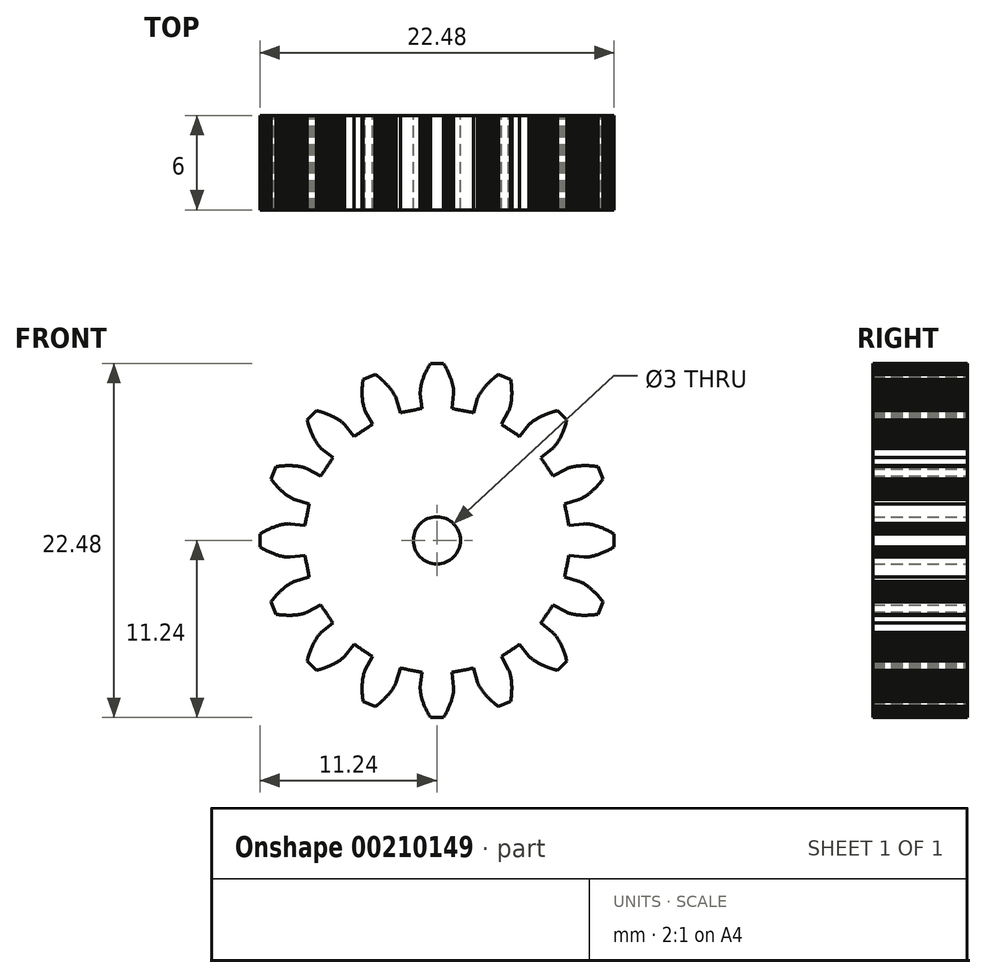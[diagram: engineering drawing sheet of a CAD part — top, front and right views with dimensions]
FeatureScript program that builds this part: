
annotation { "Feature Type Name" : "Feature", "Feature Type Description" : "" }
export const myFeature = defineFeature(function(context is Context, id is Id, definition is map)
    precondition{}
    {
        {
            var Q0;
            Q0=qCreatedBy(makeId("Front.planeOp"),FACE);
            var sketch = newSketch(context, id + "F0", { "sketchPlane" : qUnion([Q0])});
            skLineSegment(sketch, "E0", {"start": v(8.38, -0.95) * mm, "end": v(9.34, -1.06) * mm});
            skLineSegment(sketch, "E1", {"start": v(9.34, -1.06) * mm, "end": v(9.39, -1.06) * mm});
            skLineSegment(sketch, "E2", {"start": v(9.39, -1.06) * mm, "end": v(9.44, -1.06) * mm});
            skLineSegment(sketch, "E3", {"start": v(9.44, -1.06) * mm, "end": v(9.5, -1.06) * mm});
            skLineSegment(sketch, "E4", {"start": v(9.5, -1.06) * mm, "end": v(9.56, -1.05) * mm});
            skLineSegment(sketch, "E5", {"start": v(9.56, -1.05) * mm, "end": v(9.62, -1.05) * mm});
            skLineSegment(sketch, "E6", {"start": v(9.62, -1.05) * mm, "end": v(9.68, -1.04) * mm});
            skLineSegment(sketch, "E7", {"start": v(9.68, -1.04) * mm, "end": v(9.75, -1.03) * mm});
            skLineSegment(sketch, "E8", {"start": v(9.75, -1.03) * mm, "end": v(9.82, -1.01) * mm});
            skLineSegment(sketch, "E9", {"start": v(9.82, -1.01) * mm, "end": v(9.88, -1) * mm});
            skLineSegment(sketch, "E10", {"start": v(9.88, -1) * mm, "end": v(9.93, -0.99) * mm});
            skLineSegment(sketch, "E11", {"start": v(9.93, -0.99) * mm, "end": v(9.99, -0.97) * mm});
            skLineSegment(sketch, "E12", {"start": v(9.99, -0.97) * mm, "end": v(10.05, -0.95) * mm});
            skLineSegment(sketch, "E13", {"start": v(10.05, -0.95) * mm, "end": v(10.11, -0.93) * mm});
            skLineSegment(sketch, "E14", {"start": v(10.11, -0.93) * mm, "end": v(10.18, -0.91) * mm});
            skLineSegment(sketch, "E15", {"start": v(10.18, -0.91) * mm, "end": v(10.25, -0.9) * mm});
            skLineSegment(sketch, "E16", {"start": v(10.25, -0.9) * mm, "end": v(10.32, -0.87) * mm});
            skLineSegment(sketch, "E17", {"start": v(10.32, -0.87) * mm, "end": v(10.39, -0.84) * mm});
            skLineSegment(sketch, "E18", {"start": v(10.39, -0.84) * mm, "end": v(10.46, -0.8) * mm});
            skLineSegment(sketch, "E19", {"start": v(10.46, -0.8) * mm, "end": v(10.54, -0.78) * mm});
            skLineSegment(sketch, "E20", {"start": v(10.54, -0.78) * mm, "end": v(10.62, -0.74) * mm});
            skLineSegment(sketch, "E21", {"start": v(10.62, -0.74) * mm, "end": v(10.7, -0.7) * mm});
            skLineSegment(sketch, "E22", {"start": v(10.7, -0.7) * mm, "end": v(10.78, -0.67) * mm});
            skLineSegment(sketch, "E23", {"start": v(10.78, -0.67) * mm, "end": v(10.87, -0.63) * mm});
            skLineSegment(sketch, "E24", {"start": v(10.87, -0.63) * mm, "end": v(10.95, -0.58) * mm});
            skLineSegment(sketch, "E25", {"start": v(10.95, -0.58) * mm, "end": v(11.04, -0.53) * mm});
            skLineSegment(sketch, "E26", {"start": v(11.04, -0.53) * mm, "end": v(11.09, -0.5) * mm});
            skLineSegment(sketch, "E27", {"start": v(11.09, -0.5) * mm, "end": v(11.13, -0.48) * mm});
            skLineSegment(sketch, "E28", {"start": v(11.13, -0.48) * mm, "end": v(11.18, -0.46) * mm});
            skLineSegment(sketch, "E29", {"start": v(11.18, -0.46) * mm, "end": v(11.24, -0.42) * mm});
            skLineSegment(sketch, "E30", {"start": v(11.24, -0.42) * mm, "end": v(11.24, 0.42) * mm});
            skLineSegment(sketch, "E31", {"start": v(11.24, 0.42) * mm, "end": v(11.18, 0.46) * mm});
            skLineSegment(sketch, "E32", {"start": v(11.18, 0.46) * mm, "end": v(11.13, 0.48) * mm});
            skLineSegment(sketch, "E33", {"start": v(11.13, 0.48) * mm, "end": v(11.09, 0.5) * mm});
            skLineSegment(sketch, "E34", {"start": v(11.09, 0.5) * mm, "end": v(11.04, 0.53) * mm});
            skLineSegment(sketch, "E35", {"start": v(11.04, 0.53) * mm, "end": v(10.95, 0.58) * mm});
            skLineSegment(sketch, "E36", {"start": v(10.95, 0.58) * mm, "end": v(10.87, 0.63) * mm});
            skLineSegment(sketch, "E37", {"start": v(10.87, 0.63) * mm, "end": v(10.78, 0.67) * mm});
            skLineSegment(sketch, "E38", {"start": v(10.78, 0.67) * mm, "end": v(10.7, 0.7) * mm});
            skLineSegment(sketch, "E39", {"start": v(10.7, 0.7) * mm, "end": v(10.62, 0.74) * mm});
            skLineSegment(sketch, "E40", {"start": v(10.62, 0.74) * mm, "end": v(10.54, 0.78) * mm});
            skLineSegment(sketch, "E41", {"start": v(10.54, 0.78) * mm, "end": v(10.46, 0.8) * mm});
            skLineSegment(sketch, "E42", {"start": v(10.46, 0.8) * mm, "end": v(10.39, 0.84) * mm});
            skLineSegment(sketch, "E43", {"start": v(10.39, 0.84) * mm, "end": v(10.32, 0.87) * mm});
            skLineSegment(sketch, "E44", {"start": v(10.32, 0.87) * mm, "end": v(10.25, 0.9) * mm});
            skLineSegment(sketch, "E45", {"start": v(10.25, 0.9) * mm, "end": v(10.18, 0.91) * mm});
            skLineSegment(sketch, "E46", {"start": v(10.18, 0.91) * mm, "end": v(10.11, 0.93) * mm});
            skLineSegment(sketch, "E47", {"start": v(10.11, 0.93) * mm, "end": v(10.05, 0.95) * mm});
            skLineSegment(sketch, "E48", {"start": v(10.05, 0.95) * mm, "end": v(9.99, 0.97) * mm});
            skLineSegment(sketch, "E49", {"start": v(9.99, 0.97) * mm, "end": v(9.93, 0.99) * mm});
            skLineSegment(sketch, "E50", {"start": v(9.93, 0.99) * mm, "end": v(9.88, 1) * mm});
            skLineSegment(sketch, "E51", {"start": v(9.88, 1) * mm, "end": v(9.82, 1.01) * mm});
            skLineSegment(sketch, "E52", {"start": v(9.82, 1.01) * mm, "end": v(9.75, 1.03) * mm});
            skLineSegment(sketch, "E53", {"start": v(9.75, 1.03) * mm, "end": v(9.68, 1.04) * mm});
            skLineSegment(sketch, "E54", {"start": v(9.68, 1.04) * mm, "end": v(9.62, 1.05) * mm});
            skLineSegment(sketch, "E55", {"start": v(9.62, 1.05) * mm, "end": v(9.56, 1.05) * mm});
            skLineSegment(sketch, "E56", {"start": v(9.56, 1.05) * mm, "end": v(9.5, 1.06) * mm});
            skLineSegment(sketch, "E57", {"start": v(9.5, 1.06) * mm, "end": v(9.44, 1.06) * mm});
            skLineSegment(sketch, "E58", {"start": v(9.44, 1.06) * mm, "end": v(9.39, 1.06) * mm});
            skLineSegment(sketch, "E59", {"start": v(9.39, 1.06) * mm, "end": v(9.34, 1.06) * mm});
            skLineSegment(sketch, "E60", {"start": v(9.34, 1.06) * mm, "end": v(8.38, 0.95) * mm});
            skArc(sketch, "E61", {"start": v(8.38, 0.95) * mm, "mid": v(8.25, 1.64) * mm, "end": v(8.1, 2.33) * mm});
            skLineSegment(sketch, "E62", {"start": v(8.1, 2.33) * mm, "end": v(9.03, 2.6) * mm});
            skLineSegment(sketch, "E63", {"start": v(9.03, 2.6) * mm, "end": v(9.08, 2.61) * mm});
            skLineSegment(sketch, "E64", {"start": v(9.08, 2.61) * mm, "end": v(9.13, 2.63) * mm});
            skLineSegment(sketch, "E65", {"start": v(9.13, 2.63) * mm, "end": v(9.18, 2.65) * mm});
            skLineSegment(sketch, "E66", {"start": v(9.18, 2.65) * mm, "end": v(9.24, 2.69) * mm});
            skLineSegment(sketch, "E67", {"start": v(9.24, 2.69) * mm, "end": v(9.29, 2.71) * mm});
            skLineSegment(sketch, "E68", {"start": v(9.29, 2.71) * mm, "end": v(9.34, 2.75) * mm});
            skLineSegment(sketch, "E69", {"start": v(9.34, 2.75) * mm, "end": v(9.4, 2.78) * mm});
            skLineSegment(sketch, "E70", {"start": v(9.4, 2.78) * mm, "end": v(9.46, 2.83) * mm});
            skLineSegment(sketch, "E71", {"start": v(9.46, 2.83) * mm, "end": v(9.5, 2.86) * mm});
            skLineSegment(sketch, "E72", {"start": v(9.5, 2.86) * mm, "end": v(9.55, 2.9) * mm});
            skLineSegment(sketch, "E73", {"start": v(9.55, 2.9) * mm, "end": v(9.6, 2.93) * mm});
            skLineSegment(sketch, "E74", {"start": v(9.6, 2.93) * mm, "end": v(9.65, 2.97) * mm});
            skLineSegment(sketch, "E75", {"start": v(9.65, 2.97) * mm, "end": v(9.7, 3) * mm});
            skLineSegment(sketch, "E76", {"start": v(9.7, 3) * mm, "end": v(9.75, 3.05) * mm});
            skLineSegment(sketch, "E77", {"start": v(9.75, 3.05) * mm, "end": v(9.8, 3.1) * mm});
            skLineSegment(sketch, "E78", {"start": v(9.8, 3.1) * mm, "end": v(9.86, 3.15) * mm});
            skLineSegment(sketch, "E79", {"start": v(9.86, 3.15) * mm, "end": v(9.92, 3.2) * mm});
            skLineSegment(sketch, "E80", {"start": v(9.92, 3.2) * mm, "end": v(9.98, 3.26) * mm});
            skLineSegment(sketch, "E81", {"start": v(9.98, 3.26) * mm, "end": v(10.04, 3.31) * mm});
            skLineSegment(sketch, "E82", {"start": v(10.04, 3.31) * mm, "end": v(10.1, 3.38) * mm});
            skLineSegment(sketch, "E83", {"start": v(10.1, 3.38) * mm, "end": v(10.16, 3.44) * mm});
            skLineSegment(sketch, "E84", {"start": v(10.16, 3.44) * mm, "end": v(10.22, 3.5) * mm});
            skLineSegment(sketch, "E85", {"start": v(10.22, 3.5) * mm, "end": v(10.28, 3.58) * mm});
            skLineSegment(sketch, "E86", {"start": v(10.28, 3.58) * mm, "end": v(10.34, 3.66) * mm});
            skLineSegment(sketch, "E87", {"start": v(10.34, 3.66) * mm, "end": v(10.4, 3.73) * mm});
            skLineSegment(sketch, "E88", {"start": v(10.4, 3.73) * mm, "end": v(10.44, 3.77) * mm});
            skLineSegment(sketch, "E89", {"start": v(10.44, 3.77) * mm, "end": v(10.47, 3.81) * mm});
            skLineSegment(sketch, "E90", {"start": v(10.47, 3.81) * mm, "end": v(10.5, 3.86) * mm});
            skLineSegment(sketch, "E91", {"start": v(10.5, 3.86) * mm, "end": v(10.55, 3.92) * mm});
            skLineSegment(sketch, "E92", {"start": v(10.55, 3.92) * mm, "end": v(10.23, 4.69) * mm});
            skLineSegment(sketch, "E93", {"start": v(10.23, 4.69) * mm, "end": v(10.15, 4.7) * mm});
            skLineSegment(sketch, "E94", {"start": v(10.15, 4.7) * mm, "end": v(10.1, 4.7) * mm});
            skLineSegment(sketch, "E95", {"start": v(10.1, 4.7) * mm, "end": v(10.05, 4.71) * mm});
            skLineSegment(sketch, "E96", {"start": v(10.05, 4.71) * mm, "end": v(10, 4.72) * mm});
            skLineSegment(sketch, "E97", {"start": v(10, 4.72) * mm, "end": v(9.9, 4.73) * mm});
            skLineSegment(sketch, "E98", {"start": v(9.9, 4.73) * mm, "end": v(9.8, 4.74) * mm});
            skLineSegment(sketch, "E99", {"start": v(9.8, 4.74) * mm, "end": v(9.7, 4.74) * mm});
            skLineSegment(sketch, "E100", {"start": v(9.7, 4.74) * mm, "end": v(9.62, 4.75) * mm});
            skLineSegment(sketch, "E101", {"start": v(9.62, 4.75) * mm, "end": v(9.53, 4.75) * mm});
            skLineSegment(sketch, "E102", {"start": v(9.53, 4.75) * mm, "end": v(9.44, 4.75) * mm});
            skLineSegment(sketch, "E103", {"start": v(9.44, 4.75) * mm, "end": v(9.36, 4.75) * mm});
            skLineSegment(sketch, "E104", {"start": v(9.36, 4.75) * mm, "end": v(9.28, 4.75) * mm});
            skLineSegment(sketch, "E105", {"start": v(9.28, 4.75) * mm, "end": v(9.2, 4.75) * mm});
            skLineSegment(sketch, "E106", {"start": v(9.2, 4.75) * mm, "end": v(9.13, 4.74) * mm});
            skLineSegment(sketch, "E107", {"start": v(9.13, 4.74) * mm, "end": v(9.05, 4.74) * mm});
            skLineSegment(sketch, "E108", {"start": v(9.05, 4.74) * mm, "end": v(8.99, 4.73) * mm});
            skLineSegment(sketch, "E109", {"start": v(8.99, 4.73) * mm, "end": v(8.92, 4.73) * mm});
            skLineSegment(sketch, "E110", {"start": v(8.92, 4.73) * mm, "end": v(8.86, 4.72) * mm});
            skLineSegment(sketch, "E111", {"start": v(8.86, 4.72) * mm, "end": v(8.8, 4.71) * mm});
            skLineSegment(sketch, "E112", {"start": v(8.8, 4.71) * mm, "end": v(8.74, 4.7) * mm});
            skLineSegment(sketch, "E113", {"start": v(8.74, 4.7) * mm, "end": v(8.69, 4.7) * mm});
            skLineSegment(sketch, "E114", {"start": v(8.69, 4.7) * mm, "end": v(8.61, 4.68) * mm});
            skLineSegment(sketch, "E115", {"start": v(8.61, 4.68) * mm, "end": v(8.55, 4.66) * mm});
            skLineSegment(sketch, "E116", {"start": v(8.55, 4.66) * mm, "end": v(8.48, 4.65) * mm});
            skLineSegment(sketch, "E117", {"start": v(8.48, 4.65) * mm, "end": v(8.43, 4.63) * mm});
            skLineSegment(sketch, "E118", {"start": v(8.43, 4.63) * mm, "end": v(8.37, 4.61) * mm});
            skLineSegment(sketch, "E119", {"start": v(8.37, 4.61) * mm, "end": v(8.32, 4.6) * mm});
            skLineSegment(sketch, "E120", {"start": v(8.32, 4.6) * mm, "end": v(8.27, 4.57) * mm});
            skLineSegment(sketch, "E121", {"start": v(8.27, 4.57) * mm, "end": v(8.22, 4.55) * mm});
            skLineSegment(sketch, "E122", {"start": v(8.22, 4.55) * mm, "end": v(7.38, 4.09) * mm});
            skArc(sketch, "E123", {"start": v(7.38, 4.09) * mm, "mid": v(7, 4.67) * mm, "end": v(6.6, 5.25) * mm});
            skLineSegment(sketch, "E124", {"start": v(6.6, 5.25) * mm, "end": v(7.35, 5.85) * mm});
            skLineSegment(sketch, "E125", {"start": v(7.35, 5.85) * mm, "end": v(7.39, 5.89) * mm});
            skLineSegment(sketch, "E126", {"start": v(7.39, 5.89) * mm, "end": v(7.43, 5.92) * mm});
            skLineSegment(sketch, "E127", {"start": v(7.43, 5.92) * mm, "end": v(7.46, 5.96) * mm});
            skLineSegment(sketch, "E128", {"start": v(7.46, 5.96) * mm, "end": v(7.5, 6.02) * mm});
            skLineSegment(sketch, "E129", {"start": v(7.5, 6.02) * mm, "end": v(7.54, 6.06) * mm});
            skLineSegment(sketch, "E130", {"start": v(7.54, 6.06) * mm, "end": v(7.58, 6.11) * mm});
            skLineSegment(sketch, "E131", {"start": v(7.58, 6.11) * mm, "end": v(7.62, 6.17) * mm});
            skLineSegment(sketch, "E132", {"start": v(7.62, 6.17) * mm, "end": v(7.66, 6.23) * mm});
            skLineSegment(sketch, "E133", {"start": v(7.66, 6.23) * mm, "end": v(7.69, 6.28) * mm});
            skLineSegment(sketch, "E134", {"start": v(7.69, 6.28) * mm, "end": v(7.72, 6.33) * mm});
            skLineSegment(sketch, "E135", {"start": v(7.72, 6.33) * mm, "end": v(7.75, 6.38) * mm});
            skLineSegment(sketch, "E136", {"start": v(7.75, 6.38) * mm, "end": v(7.78, 6.43) * mm});
            skLineSegment(sketch, "E137", {"start": v(7.78, 6.43) * mm, "end": v(7.81, 6.5) * mm});
            skLineSegment(sketch, "E138", {"start": v(7.81, 6.5) * mm, "end": v(7.84, 6.55) * mm});
            skLineSegment(sketch, "E139", {"start": v(7.84, 6.55) * mm, "end": v(7.88, 6.62) * mm});
            skLineSegment(sketch, "E140", {"start": v(7.88, 6.62) * mm, "end": v(7.9, 6.68) * mm});
            skLineSegment(sketch, "E141", {"start": v(7.9, 6.68) * mm, "end": v(7.94, 6.75) * mm});
            skLineSegment(sketch, "E142", {"start": v(7.94, 6.75) * mm, "end": v(7.97, 6.83) * mm});
            skLineSegment(sketch, "E143", {"start": v(7.97, 6.83) * mm, "end": v(8, 6.9) * mm});
            skLineSegment(sketch, "E144", {"start": v(8, 6.9) * mm, "end": v(8.04, 6.98) * mm});
            skLineSegment(sketch, "E145", {"start": v(8.04, 6.98) * mm, "end": v(8.07, 7.07) * mm});
            skLineSegment(sketch, "E146", {"start": v(8.07, 7.07) * mm, "end": v(8.1, 7.15) * mm});
            skLineSegment(sketch, "E147", {"start": v(8.1, 7.15) * mm, "end": v(8.13, 7.24) * mm});
            skLineSegment(sketch, "E148", {"start": v(8.13, 7.24) * mm, "end": v(8.16, 7.33) * mm});
            skLineSegment(sketch, "E149", {"start": v(8.16, 7.33) * mm, "end": v(8.18, 7.43) * mm});
            skLineSegment(sketch, "E150", {"start": v(8.18, 7.43) * mm, "end": v(8.2, 7.48) * mm});
            skLineSegment(sketch, "E151", {"start": v(8.2, 7.48) * mm, "end": v(8.21, 7.53) * mm});
            skLineSegment(sketch, "E152", {"start": v(8.21, 7.53) * mm, "end": v(8.23, 7.58) * mm});
            skLineSegment(sketch, "E153", {"start": v(8.23, 7.58) * mm, "end": v(8.24, 7.66) * mm});
            skLineSegment(sketch, "E154", {"start": v(8.24, 7.66) * mm, "end": v(7.66, 8.24) * mm});
            skLineSegment(sketch, "E155", {"start": v(7.66, 8.24) * mm, "end": v(7.58, 8.23) * mm});
            skLineSegment(sketch, "E156", {"start": v(7.58, 8.23) * mm, "end": v(7.53, 8.21) * mm});
            skLineSegment(sketch, "E157", {"start": v(7.53, 8.21) * mm, "end": v(7.48, 8.2) * mm});
            skLineSegment(sketch, "E158", {"start": v(7.48, 8.2) * mm, "end": v(7.43, 8.18) * mm});
            skLineSegment(sketch, "E159", {"start": v(7.43, 8.18) * mm, "end": v(7.33, 8.16) * mm});
            skLineSegment(sketch, "E160", {"start": v(7.33, 8.16) * mm, "end": v(7.24, 8.13) * mm});
            skLineSegment(sketch, "E161", {"start": v(7.24, 8.13) * mm, "end": v(7.15, 8.1) * mm});
            skLineSegment(sketch, "E162", {"start": v(7.15, 8.1) * mm, "end": v(7.07, 8.07) * mm});
            skLineSegment(sketch, "E163", {"start": v(7.07, 8.07) * mm, "end": v(6.98, 8.04) * mm});
            skLineSegment(sketch, "E164", {"start": v(6.98, 8.04) * mm, "end": v(6.9, 8) * mm});
            skLineSegment(sketch, "E165", {"start": v(6.9, 8) * mm, "end": v(6.83, 7.97) * mm});
            skLineSegment(sketch, "E166", {"start": v(6.83, 7.97) * mm, "end": v(6.75, 7.94) * mm});
            skLineSegment(sketch, "E167", {"start": v(6.75, 7.94) * mm, "end": v(6.68, 7.9) * mm});
            skLineSegment(sketch, "E168", {"start": v(6.68, 7.9) * mm, "end": v(6.62, 7.88) * mm});
            skLineSegment(sketch, "E169", {"start": v(6.62, 7.88) * mm, "end": v(6.55, 7.84) * mm});
            skLineSegment(sketch, "E170", {"start": v(6.55, 7.84) * mm, "end": v(6.5, 7.81) * mm});
            skLineSegment(sketch, "E171", {"start": v(6.5, 7.81) * mm, "end": v(6.43, 7.78) * mm});
            skLineSegment(sketch, "E172", {"start": v(6.43, 7.78) * mm, "end": v(6.38, 7.75) * mm});
            skLineSegment(sketch, "E173", {"start": v(6.38, 7.75) * mm, "end": v(6.33, 7.72) * mm});
            skLineSegment(sketch, "E174", {"start": v(6.33, 7.72) * mm, "end": v(6.28, 7.69) * mm});
            skLineSegment(sketch, "E175", {"start": v(6.28, 7.69) * mm, "end": v(6.23, 7.66) * mm});
            skLineSegment(sketch, "E176", {"start": v(6.23, 7.66) * mm, "end": v(6.17, 7.62) * mm});
            skLineSegment(sketch, "E177", {"start": v(6.17, 7.62) * mm, "end": v(6.11, 7.58) * mm});
            skLineSegment(sketch, "E178", {"start": v(6.11, 7.58) * mm, "end": v(6.06, 7.54) * mm});
            skLineSegment(sketch, "E179", {"start": v(6.06, 7.54) * mm, "end": v(6.02, 7.5) * mm});
            skLineSegment(sketch, "E180", {"start": v(6.02, 7.5) * mm, "end": v(5.96, 7.46) * mm});
            skLineSegment(sketch, "E181", {"start": v(5.96, 7.46) * mm, "end": v(5.92, 7.43) * mm});
            skLineSegment(sketch, "E182", {"start": v(5.92, 7.43) * mm, "end": v(5.89, 7.39) * mm});
            skLineSegment(sketch, "E183", {"start": v(5.89, 7.39) * mm, "end": v(5.85, 7.35) * mm});
            skLineSegment(sketch, "E184", {"start": v(5.85, 7.35) * mm, "end": v(5.25, 6.6) * mm});
            skArc(sketch, "E185", {"start": v(5.25, 6.6) * mm, "mid": v(4.67, 7) * mm, "end": v(4.09, 7.38) * mm});
            skLineSegment(sketch, "E186", {"start": v(4.09, 7.38) * mm, "end": v(4.55, 8.22) * mm});
            skLineSegment(sketch, "E187", {"start": v(4.55, 8.22) * mm, "end": v(4.57, 8.27) * mm});
            skLineSegment(sketch, "E188", {"start": v(4.57, 8.27) * mm, "end": v(4.6, 8.32) * mm});
            skLineSegment(sketch, "E189", {"start": v(4.6, 8.32) * mm, "end": v(4.61, 8.37) * mm});
            skLineSegment(sketch, "E190", {"start": v(4.61, 8.37) * mm, "end": v(4.63, 8.43) * mm});
            skLineSegment(sketch, "E191", {"start": v(4.63, 8.43) * mm, "end": v(4.65, 8.48) * mm});
            skLineSegment(sketch, "E192", {"start": v(4.65, 8.48) * mm, "end": v(4.66, 8.55) * mm});
            skLineSegment(sketch, "E193", {"start": v(4.66, 8.55) * mm, "end": v(4.68, 8.61) * mm});
            skLineSegment(sketch, "E194", {"start": v(4.68, 8.61) * mm, "end": v(4.7, 8.69) * mm});
            skLineSegment(sketch, "E195", {"start": v(4.7, 8.69) * mm, "end": v(4.7, 8.74) * mm});
            skLineSegment(sketch, "E196", {"start": v(4.7, 8.74) * mm, "end": v(4.71, 8.8) * mm});
            skLineSegment(sketch, "E197", {"start": v(4.71, 8.8) * mm, "end": v(4.72, 8.86) * mm});
            skLineSegment(sketch, "E198", {"start": v(4.72, 8.86) * mm, "end": v(4.73, 8.92) * mm});
            skLineSegment(sketch, "E199", {"start": v(4.73, 8.92) * mm, "end": v(4.73, 8.99) * mm});
            skLineSegment(sketch, "E200", {"start": v(4.73, 8.99) * mm, "end": v(4.74, 9.05) * mm});
            skLineSegment(sketch, "E201", {"start": v(4.74, 9.05) * mm, "end": v(4.74, 9.13) * mm});
            skLineSegment(sketch, "E202", {"start": v(4.74, 9.13) * mm, "end": v(4.75, 9.2) * mm});
            skLineSegment(sketch, "E203", {"start": v(4.75, 9.2) * mm, "end": v(4.75, 9.28) * mm});
            skLineSegment(sketch, "E204", {"start": v(4.75, 9.28) * mm, "end": v(4.75, 9.36) * mm});
            skLineSegment(sketch, "E205", {"start": v(4.75, 9.36) * mm, "end": v(4.75, 9.44) * mm});
            skLineSegment(sketch, "E206", {"start": v(4.75, 9.44) * mm, "end": v(4.75, 9.53) * mm});
            skLineSegment(sketch, "E207", {"start": v(4.75, 9.53) * mm, "end": v(4.75, 9.62) * mm});
            skLineSegment(sketch, "E208", {"start": v(4.75, 9.62) * mm, "end": v(4.74, 9.7) * mm});
            skLineSegment(sketch, "E209", {"start": v(4.74, 9.7) * mm, "end": v(4.74, 9.8) * mm});
            skLineSegment(sketch, "E210", {"start": v(4.74, 9.8) * mm, "end": v(4.73, 9.9) * mm});
            skLineSegment(sketch, "E211", {"start": v(4.73, 9.9) * mm, "end": v(4.72, 10) * mm});
            skLineSegment(sketch, "E212", {"start": v(4.72, 10) * mm, "end": v(4.71, 10.05) * mm});
            skLineSegment(sketch, "E213", {"start": v(4.71, 10.05) * mm, "end": v(4.7, 10.1) * mm});
            skLineSegment(sketch, "E214", {"start": v(4.7, 10.1) * mm, "end": v(4.7, 10.15) * mm});
            skLineSegment(sketch, "E215", {"start": v(4.7, 10.15) * mm, "end": v(4.69, 10.23) * mm});
            skLineSegment(sketch, "E216", {"start": v(4.69, 10.23) * mm, "end": v(3.92, 10.55) * mm});
            skLineSegment(sketch, "E217", {"start": v(3.92, 10.55) * mm, "end": v(3.86, 10.5) * mm});
            skLineSegment(sketch, "E218", {"start": v(3.86, 10.5) * mm, "end": v(3.81, 10.47) * mm});
            skLineSegment(sketch, "E219", {"start": v(3.81, 10.47) * mm, "end": v(3.77, 10.44) * mm});
            skLineSegment(sketch, "E220", {"start": v(3.77, 10.44) * mm, "end": v(3.73, 10.4) * mm});
            skLineSegment(sketch, "E221", {"start": v(3.73, 10.4) * mm, "end": v(3.66, 10.34) * mm});
            skLineSegment(sketch, "E222", {"start": v(3.66, 10.34) * mm, "end": v(3.58, 10.28) * mm});
            skLineSegment(sketch, "E223", {"start": v(3.58, 10.28) * mm, "end": v(3.5, 10.22) * mm});
            skLineSegment(sketch, "E224", {"start": v(3.5, 10.22) * mm, "end": v(3.44, 10.16) * mm});
            skLineSegment(sketch, "E225", {"start": v(3.44, 10.16) * mm, "end": v(3.38, 10.1) * mm});
            skLineSegment(sketch, "E226", {"start": v(3.38, 10.1) * mm, "end": v(3.31, 10.04) * mm});
            skLineSegment(sketch, "E227", {"start": v(3.31, 10.04) * mm, "end": v(3.26, 9.98) * mm});
            skLineSegment(sketch, "E228", {"start": v(3.26, 9.98) * mm, "end": v(3.2, 9.92) * mm});
            skLineSegment(sketch, "E229", {"start": v(3.2, 9.92) * mm, "end": v(3.15, 9.86) * mm});
            skLineSegment(sketch, "E230", {"start": v(3.15, 9.86) * mm, "end": v(3.1, 9.8) * mm});
            skLineSegment(sketch, "E231", {"start": v(3.1, 9.8) * mm, "end": v(3.05, 9.75) * mm});
            skLineSegment(sketch, "E232", {"start": v(3.05, 9.75) * mm, "end": v(3, 9.7) * mm});
            skLineSegment(sketch, "E233", {"start": v(3, 9.7) * mm, "end": v(2.97, 9.65) * mm});
            skLineSegment(sketch, "E234", {"start": v(2.97, 9.65) * mm, "end": v(2.93, 9.6) * mm});
            skLineSegment(sketch, "E235", {"start": v(2.93, 9.6) * mm, "end": v(2.9, 9.55) * mm});
            skLineSegment(sketch, "E236", {"start": v(2.9, 9.55) * mm, "end": v(2.86, 9.5) * mm});
            skLineSegment(sketch, "E237", {"start": v(2.86, 9.5) * mm, "end": v(2.83, 9.46) * mm});
            skLineSegment(sketch, "E238", {"start": v(2.83, 9.46) * mm, "end": v(2.78, 9.4) * mm});
            skLineSegment(sketch, "E239", {"start": v(2.78, 9.4) * mm, "end": v(2.75, 9.34) * mm});
            skLineSegment(sketch, "E240", {"start": v(2.75, 9.34) * mm, "end": v(2.71, 9.29) * mm});
            skLineSegment(sketch, "E241", {"start": v(2.71, 9.29) * mm, "end": v(2.69, 9.24) * mm});
            skLineSegment(sketch, "E242", {"start": v(2.69, 9.24) * mm, "end": v(2.65, 9.18) * mm});
            skLineSegment(sketch, "E243", {"start": v(2.65, 9.18) * mm, "end": v(2.63, 9.13) * mm});
            skLineSegment(sketch, "E244", {"start": v(2.63, 9.13) * mm, "end": v(2.61, 9.08) * mm});
            skLineSegment(sketch, "E245", {"start": v(2.61, 9.08) * mm, "end": v(2.6, 9.03) * mm});
            skLineSegment(sketch, "E246", {"start": v(2.6, 9.03) * mm, "end": v(2.33, 8.1) * mm});
            skArc(sketch, "E247", {"start": v(2.33, 8.1) * mm, "mid": v(1.64, 8.25) * mm, "end": v(0.95, 8.38) * mm});
            skLineSegment(sketch, "E248", {"start": v(0.95, 8.38) * mm, "end": v(1.06, 9.34) * mm});
            skLineSegment(sketch, "E249", {"start": v(1.06, 9.34) * mm, "end": v(1.06, 9.39) * mm});
            skLineSegment(sketch, "E250", {"start": v(1.06, 9.39) * mm, "end": v(1.06, 9.44) * mm});
            skLineSegment(sketch, "E251", {"start": v(1.06, 9.44) * mm, "end": v(1.06, 9.5) * mm});
            skLineSegment(sketch, "E252", {"start": v(1.06, 9.5) * mm, "end": v(1.05, 9.56) * mm});
            skLineSegment(sketch, "E253", {"start": v(1.05, 9.56) * mm, "end": v(1.05, 9.62) * mm});
            skLineSegment(sketch, "E254", {"start": v(1.05, 9.62) * mm, "end": v(1.04, 9.68) * mm});
            skLineSegment(sketch, "E255", {"start": v(1.04, 9.68) * mm, "end": v(1.03, 9.75) * mm});
            skLineSegment(sketch, "E256", {"start": v(1.03, 9.75) * mm, "end": v(1.01, 9.82) * mm});
            skLineSegment(sketch, "E257", {"start": v(1.01, 9.82) * mm, "end": v(1, 9.88) * mm});
            skLineSegment(sketch, "E258", {"start": v(1, 9.88) * mm, "end": v(0.99, 9.93) * mm});
            skLineSegment(sketch, "E259", {"start": v(0.99, 9.93) * mm, "end": v(0.97, 9.99) * mm});
            skLineSegment(sketch, "E260", {"start": v(0.97, 9.99) * mm, "end": v(0.95, 10.05) * mm});
            skLineSegment(sketch, "E261", {"start": v(0.95, 10.05) * mm, "end": v(0.93, 10.11) * mm});
            skLineSegment(sketch, "E262", {"start": v(0.93, 10.11) * mm, "end": v(0.91, 10.18) * mm});
            skLineSegment(sketch, "E263", {"start": v(0.91, 10.18) * mm, "end": v(0.9, 10.25) * mm});
            skLineSegment(sketch, "E264", {"start": v(0.9, 10.25) * mm, "end": v(0.87, 10.32) * mm});
            skLineSegment(sketch, "E265", {"start": v(0.87, 10.32) * mm, "end": v(0.84, 10.39) * mm});
            skLineSegment(sketch, "E266", {"start": v(0.84, 10.39) * mm, "end": v(0.8, 10.46) * mm});
            skLineSegment(sketch, "E267", {"start": v(0.8, 10.46) * mm, "end": v(0.78, 10.54) * mm});
            skLineSegment(sketch, "E268", {"start": v(0.78, 10.54) * mm, "end": v(0.74, 10.62) * mm});
            skLineSegment(sketch, "E269", {"start": v(0.74, 10.62) * mm, "end": v(0.7, 10.7) * mm});
            skLineSegment(sketch, "E270", {"start": v(0.7, 10.7) * mm, "end": v(0.67, 10.78) * mm});
            skLineSegment(sketch, "E271", {"start": v(0.67, 10.78) * mm, "end": v(0.63, 10.87) * mm});
            skLineSegment(sketch, "E272", {"start": v(0.63, 10.87) * mm, "end": v(0.58, 10.95) * mm});
            skLineSegment(sketch, "E273", {"start": v(0.58, 10.95) * mm, "end": v(0.53, 11.04) * mm});
            skLineSegment(sketch, "E274", {"start": v(0.53, 11.04) * mm, "end": v(0.5, 11.09) * mm});
            skLineSegment(sketch, "E275", {"start": v(0.5, 11.09) * mm, "end": v(0.48, 11.13) * mm});
            skLineSegment(sketch, "E276", {"start": v(0.48, 11.13) * mm, "end": v(0.46, 11.18) * mm});
            skLineSegment(sketch, "E277", {"start": v(0.46, 11.18) * mm, "end": v(0.42, 11.24) * mm});
            skLineSegment(sketch, "E278", {"start": v(0.42, 11.24) * mm, "end": v(-0.42, 11.24) * mm});
            skLineSegment(sketch, "E279", {"start": v(-0.42, 11.24) * mm, "end": v(-0.46, 11.18) * mm});
            skLineSegment(sketch, "E280", {"start": v(-0.46, 11.18) * mm, "end": v(-0.48, 11.13) * mm});
            skLineSegment(sketch, "E281", {"start": v(-0.48, 11.13) * mm, "end": v(-0.5, 11.09) * mm});
            skLineSegment(sketch, "E282", {"start": v(-0.5, 11.09) * mm, "end": v(-0.53, 11.04) * mm});
            skLineSegment(sketch, "E283", {"start": v(-0.53, 11.04) * mm, "end": v(-0.58, 10.95) * mm});
            skLineSegment(sketch, "E284", {"start": v(-0.58, 10.95) * mm, "end": v(-0.63, 10.87) * mm});
            skLineSegment(sketch, "E285", {"start": v(-0.63, 10.87) * mm, "end": v(-0.67, 10.78) * mm});
            skLineSegment(sketch, "E286", {"start": v(-0.67, 10.78) * mm, "end": v(-0.7, 10.7) * mm});
            skLineSegment(sketch, "E287", {"start": v(-0.7, 10.7) * mm, "end": v(-0.74, 10.62) * mm});
            skLineSegment(sketch, "E288", {"start": v(-0.74, 10.62) * mm, "end": v(-0.78, 10.54) * mm});
            skLineSegment(sketch, "E289", {"start": v(-0.78, 10.54) * mm, "end": v(-0.8, 10.46) * mm});
            skLineSegment(sketch, "E290", {"start": v(-0.8, 10.46) * mm, "end": v(-0.84, 10.39) * mm});
            skLineSegment(sketch, "E291", {"start": v(-0.84, 10.39) * mm, "end": v(-0.87, 10.32) * mm});
            skLineSegment(sketch, "E292", {"start": v(-0.87, 10.32) * mm, "end": v(-0.9, 10.25) * mm});
            skLineSegment(sketch, "E293", {"start": v(-0.9, 10.25) * mm, "end": v(-0.91, 10.18) * mm});
            skLineSegment(sketch, "E294", {"start": v(-0.91, 10.18) * mm, "end": v(-0.93, 10.11) * mm});
            skLineSegment(sketch, "E295", {"start": v(-0.93, 10.11) * mm, "end": v(-0.95, 10.05) * mm});
            skLineSegment(sketch, "E296", {"start": v(-0.95, 10.05) * mm, "end": v(-0.97, 9.99) * mm});
            skLineSegment(sketch, "E297", {"start": v(-0.97, 9.99) * mm, "end": v(-0.99, 9.93) * mm});
            skLineSegment(sketch, "E298", {"start": v(-0.99, 9.93) * mm, "end": v(-1, 9.88) * mm});
            skLineSegment(sketch, "E299", {"start": v(-1, 9.88) * mm, "end": v(-1.01, 9.82) * mm});
            skLineSegment(sketch, "E300", {"start": v(-1.01, 9.82) * mm, "end": v(-1.03, 9.75) * mm});
            skLineSegment(sketch, "E301", {"start": v(-1.03, 9.75) * mm, "end": v(-1.04, 9.68) * mm});
            skLineSegment(sketch, "E302", {"start": v(-1.04, 9.68) * mm, "end": v(-1.05, 9.62) * mm});
            skLineSegment(sketch, "E303", {"start": v(-1.05, 9.62) * mm, "end": v(-1.05, 9.56) * mm});
            skLineSegment(sketch, "E304", {"start": v(-1.05, 9.56) * mm, "end": v(-1.06, 9.5) * mm});
            skLineSegment(sketch, "E305", {"start": v(-1.06, 9.5) * mm, "end": v(-1.06, 9.44) * mm});
            skLineSegment(sketch, "E306", {"start": v(-1.06, 9.44) * mm, "end": v(-1.06, 9.39) * mm});
            skLineSegment(sketch, "E307", {"start": v(-1.06, 9.39) * mm, "end": v(-1.06, 9.34) * mm});
            skLineSegment(sketch, "E308", {"start": v(-1.06, 9.34) * mm, "end": v(-0.95, 8.38) * mm});
            skArc(sketch, "E309", {"start": v(-0.95, 8.38) * mm, "mid": v(-1.64, 8.25) * mm, "end": v(-2.33, 8.1) * mm});
            skLineSegment(sketch, "E310", {"start": v(-2.33, 8.1) * mm, "end": v(-2.6, 9.03) * mm});
            skLineSegment(sketch, "E311", {"start": v(-2.6, 9.03) * mm, "end": v(-2.61, 9.08) * mm});
            skLineSegment(sketch, "E312", {"start": v(-2.61, 9.08) * mm, "end": v(-2.63, 9.13) * mm});
            skLineSegment(sketch, "E313", {"start": v(-2.63, 9.13) * mm, "end": v(-2.65, 9.18) * mm});
            skLineSegment(sketch, "E314", {"start": v(-2.65, 9.18) * mm, "end": v(-2.69, 9.24) * mm});
            skLineSegment(sketch, "E315", {"start": v(-2.69, 9.24) * mm, "end": v(-2.71, 9.29) * mm});
            skLineSegment(sketch, "E316", {"start": v(-2.71, 9.29) * mm, "end": v(-2.75, 9.34) * mm});
            skLineSegment(sketch, "E317", {"start": v(-2.75, 9.34) * mm, "end": v(-2.78, 9.4) * mm});
            skLineSegment(sketch, "E318", {"start": v(-2.78, 9.4) * mm, "end": v(-2.83, 9.46) * mm});
            skLineSegment(sketch, "E319", {"start": v(-2.83, 9.46) * mm, "end": v(-2.86, 9.5) * mm});
            skLineSegment(sketch, "E320", {"start": v(-2.86, 9.5) * mm, "end": v(-2.9, 9.55) * mm});
            skLineSegment(sketch, "E321", {"start": v(-2.9, 9.55) * mm, "end": v(-2.93, 9.6) * mm});
            skLineSegment(sketch, "E322", {"start": v(-2.93, 9.6) * mm, "end": v(-2.97, 9.65) * mm});
            skLineSegment(sketch, "E323", {"start": v(-2.97, 9.65) * mm, "end": v(-3, 9.7) * mm});
            skLineSegment(sketch, "E324", {"start": v(-3, 9.7) * mm, "end": v(-3.05, 9.75) * mm});
            skLineSegment(sketch, "E325", {"start": v(-3.05, 9.75) * mm, "end": v(-3.1, 9.8) * mm});
            skLineSegment(sketch, "E326", {"start": v(-3.1, 9.8) * mm, "end": v(-3.15, 9.86) * mm});
            skLineSegment(sketch, "E327", {"start": v(-3.15, 9.86) * mm, "end": v(-3.2, 9.92) * mm});
            skLineSegment(sketch, "E328", {"start": v(-3.2, 9.92) * mm, "end": v(-3.26, 9.98) * mm});
            skLineSegment(sketch, "E329", {"start": v(-3.26, 9.98) * mm, "end": v(-3.31, 10.04) * mm});
            skLineSegment(sketch, "E330", {"start": v(-3.31, 10.04) * mm, "end": v(-3.38, 10.1) * mm});
            skLineSegment(sketch, "E331", {"start": v(-3.38, 10.1) * mm, "end": v(-3.44, 10.16) * mm});
            skLineSegment(sketch, "E332", {"start": v(-3.44, 10.16) * mm, "end": v(-3.5, 10.22) * mm});
            skLineSegment(sketch, "E333", {"start": v(-3.5, 10.22) * mm, "end": v(-3.58, 10.28) * mm});
            skLineSegment(sketch, "E334", {"start": v(-3.58, 10.28) * mm, "end": v(-3.66, 10.34) * mm});
            skLineSegment(sketch, "E335", {"start": v(-3.66, 10.34) * mm, "end": v(-3.73, 10.4) * mm});
            skLineSegment(sketch, "E336", {"start": v(-3.73, 10.4) * mm, "end": v(-3.77, 10.44) * mm});
            skLineSegment(sketch, "E337", {"start": v(-3.77, 10.44) * mm, "end": v(-3.81, 10.47) * mm});
            skLineSegment(sketch, "E338", {"start": v(-3.81, 10.47) * mm, "end": v(-3.86, 10.5) * mm});
            skLineSegment(sketch, "E339", {"start": v(-3.86, 10.5) * mm, "end": v(-3.92, 10.55) * mm});
            skLineSegment(sketch, "E340", {"start": v(-3.92, 10.55) * mm, "end": v(-4.69, 10.23) * mm});
            skLineSegment(sketch, "E341", {"start": v(-4.69, 10.23) * mm, "end": v(-4.7, 10.15) * mm});
            skLineSegment(sketch, "E342", {"start": v(-4.7, 10.15) * mm, "end": v(-4.7, 10.1) * mm});
            skLineSegment(sketch, "E343", {"start": v(-4.7, 10.1) * mm, "end": v(-4.71, 10.05) * mm});
            skLineSegment(sketch, "E344", {"start": v(-4.71, 10.05) * mm, "end": v(-4.72, 10) * mm});
            skLineSegment(sketch, "E345", {"start": v(-4.72, 10) * mm, "end": v(-4.73, 9.9) * mm});
            skLineSegment(sketch, "E346", {"start": v(-4.73, 9.9) * mm, "end": v(-4.74, 9.8) * mm});
            skLineSegment(sketch, "E347", {"start": v(-4.74, 9.8) * mm, "end": v(-4.74, 9.7) * mm});
            skLineSegment(sketch, "E348", {"start": v(-4.74, 9.7) * mm, "end": v(-4.75, 9.62) * mm});
            skLineSegment(sketch, "E349", {"start": v(-4.75, 9.62) * mm, "end": v(-4.75, 9.53) * mm});
            skLineSegment(sketch, "E350", {"start": v(-4.75, 9.53) * mm, "end": v(-4.75, 9.44) * mm});
            skLineSegment(sketch, "E351", {"start": v(-4.75, 9.44) * mm, "end": v(-4.75, 9.36) * mm});
            skLineSegment(sketch, "E352", {"start": v(-4.75, 9.36) * mm, "end": v(-4.75, 9.28) * mm});
            skLineSegment(sketch, "E353", {"start": v(-4.75, 9.28) * mm, "end": v(-4.75, 9.2) * mm});
            skLineSegment(sketch, "E354", {"start": v(-4.75, 9.2) * mm, "end": v(-4.74, 9.13) * mm});
            skLineSegment(sketch, "E355", {"start": v(-4.74, 9.13) * mm, "end": v(-4.74, 9.05) * mm});
            skLineSegment(sketch, "E356", {"start": v(-4.74, 9.05) * mm, "end": v(-4.73, 8.99) * mm});
            skLineSegment(sketch, "E357", {"start": v(-4.73, 8.99) * mm, "end": v(-4.73, 8.92) * mm});
            skLineSegment(sketch, "E358", {"start": v(-4.73, 8.92) * mm, "end": v(-4.72, 8.86) * mm});
            skLineSegment(sketch, "E359", {"start": v(-4.72, 8.86) * mm, "end": v(-4.71, 8.8) * mm});
            skLineSegment(sketch, "E360", {"start": v(-4.71, 8.8) * mm, "end": v(-4.7, 8.74) * mm});
            skLineSegment(sketch, "E361", {"start": v(-4.7, 8.74) * mm, "end": v(-4.7, 8.69) * mm});
            skLineSegment(sketch, "E362", {"start": v(-4.7, 8.69) * mm, "end": v(-4.68, 8.61) * mm});
            skLineSegment(sketch, "E363", {"start": v(-4.68, 8.61) * mm, "end": v(-4.66, 8.55) * mm});
            skLineSegment(sketch, "E364", {"start": v(-4.66, 8.55) * mm, "end": v(-4.65, 8.48) * mm});
            skLineSegment(sketch, "E365", {"start": v(-4.65, 8.48) * mm, "end": v(-4.63, 8.43) * mm});
            skLineSegment(sketch, "E366", {"start": v(-4.63, 8.43) * mm, "end": v(-4.61, 8.37) * mm});
            skLineSegment(sketch, "E367", {"start": v(-4.61, 8.37) * mm, "end": v(-4.6, 8.32) * mm});
            skLineSegment(sketch, "E368", {"start": v(-4.6, 8.32) * mm, "end": v(-4.57, 8.27) * mm});
            skLineSegment(sketch, "E369", {"start": v(-4.57, 8.27) * mm, "end": v(-4.55, 8.22) * mm});
            skLineSegment(sketch, "E370", {"start": v(-4.55, 8.22) * mm, "end": v(-4.09, 7.38) * mm});
            skArc(sketch, "E371", {"start": v(-4.09, 7.38) * mm, "mid": v(-4.67, 7) * mm, "end": v(-5.25, 6.6) * mm});
            skLineSegment(sketch, "E372", {"start": v(-5.25, 6.6) * mm, "end": v(-5.85, 7.35) * mm});
            skLineSegment(sketch, "E373", {"start": v(-5.85, 7.35) * mm, "end": v(-5.89, 7.39) * mm});
            skLineSegment(sketch, "E374", {"start": v(-5.89, 7.39) * mm, "end": v(-5.92, 7.43) * mm});
            skLineSegment(sketch, "E375", {"start": v(-5.92, 7.43) * mm, "end": v(-5.96, 7.46) * mm});
            skLineSegment(sketch, "E376", {"start": v(-5.96, 7.46) * mm, "end": v(-6.02, 7.5) * mm});
            skLineSegment(sketch, "E377", {"start": v(-6.02, 7.5) * mm, "end": v(-6.06, 7.54) * mm});
            skLineSegment(sketch, "E378", {"start": v(-6.06, 7.54) * mm, "end": v(-6.11, 7.58) * mm});
            skLineSegment(sketch, "E379", {"start": v(-6.11, 7.58) * mm, "end": v(-6.17, 7.62) * mm});
            skLineSegment(sketch, "E380", {"start": v(-6.17, 7.62) * mm, "end": v(-6.23, 7.66) * mm});
            skLineSegment(sketch, "E381", {"start": v(-6.23, 7.66) * mm, "end": v(-6.28, 7.69) * mm});
            skLineSegment(sketch, "E382", {"start": v(-6.28, 7.69) * mm, "end": v(-6.33, 7.72) * mm});
            skLineSegment(sketch, "E383", {"start": v(-6.33, 7.72) * mm, "end": v(-6.38, 7.75) * mm});
            skLineSegment(sketch, "E384", {"start": v(-6.38, 7.75) * mm, "end": v(-6.43, 7.78) * mm});
            skLineSegment(sketch, "E385", {"start": v(-6.43, 7.78) * mm, "end": v(-6.5, 7.81) * mm});
            skLineSegment(sketch, "E386", {"start": v(-6.5, 7.81) * mm, "end": v(-6.55, 7.84) * mm});
            skLineSegment(sketch, "E387", {"start": v(-6.55, 7.84) * mm, "end": v(-6.62, 7.88) * mm});
            skLineSegment(sketch, "E388", {"start": v(-6.62, 7.88) * mm, "end": v(-6.68, 7.9) * mm});
            skLineSegment(sketch, "E389", {"start": v(-6.68, 7.9) * mm, "end": v(-6.75, 7.94) * mm});
            skLineSegment(sketch, "E390", {"start": v(-6.75, 7.94) * mm, "end": v(-6.83, 7.97) * mm});
            skLineSegment(sketch, "E391", {"start": v(-6.83, 7.97) * mm, "end": v(-6.9, 8) * mm});
            skLineSegment(sketch, "E392", {"start": v(-6.9, 8) * mm, "end": v(-6.98, 8.04) * mm});
            skLineSegment(sketch, "E393", {"start": v(-6.98, 8.04) * mm, "end": v(-7.07, 8.07) * mm});
            skLineSegment(sketch, "E394", {"start": v(-7.07, 8.07) * mm, "end": v(-7.15, 8.1) * mm});
            skLineSegment(sketch, "E395", {"start": v(-7.15, 8.1) * mm, "end": v(-7.24, 8.13) * mm});
            skLineSegment(sketch, "E396", {"start": v(-7.24, 8.13) * mm, "end": v(-7.33, 8.16) * mm});
            skLineSegment(sketch, "E397", {"start": v(-7.33, 8.16) * mm, "end": v(-7.43, 8.18) * mm});
            skLineSegment(sketch, "E398", {"start": v(-7.43, 8.18) * mm, "end": v(-7.48, 8.2) * mm});
            skLineSegment(sketch, "E399", {"start": v(-7.48, 8.2) * mm, "end": v(-7.53, 8.21) * mm});
            skLineSegment(sketch, "E400", {"start": v(-7.53, 8.21) * mm, "end": v(-7.58, 8.23) * mm});
            skLineSegment(sketch, "E401", {"start": v(-7.58, 8.23) * mm, "end": v(-7.66, 8.24) * mm});
            skLineSegment(sketch, "E402", {"start": v(-7.66, 8.24) * mm, "end": v(-8.24, 7.66) * mm});
            skLineSegment(sketch, "E403", {"start": v(-8.24, 7.66) * mm, "end": v(-8.23, 7.58) * mm});
            skLineSegment(sketch, "E404", {"start": v(-8.23, 7.58) * mm, "end": v(-8.21, 7.53) * mm});
            skLineSegment(sketch, "E405", {"start": v(-8.21, 7.53) * mm, "end": v(-8.2, 7.48) * mm});
            skLineSegment(sketch, "E406", {"start": v(-8.2, 7.48) * mm, "end": v(-8.18, 7.43) * mm});
            skLineSegment(sketch, "E407", {"start": v(-8.18, 7.43) * mm, "end": v(-8.16, 7.33) * mm});
            skLineSegment(sketch, "E408", {"start": v(-8.16, 7.33) * mm, "end": v(-8.13, 7.24) * mm});
            skLineSegment(sketch, "E409", {"start": v(-8.13, 7.24) * mm, "end": v(-8.1, 7.15) * mm});
            skLineSegment(sketch, "E410", {"start": v(-8.1, 7.15) * mm, "end": v(-8.07, 7.07) * mm});
            skLineSegment(sketch, "E411", {"start": v(-8.07, 7.07) * mm, "end": v(-8.04, 6.98) * mm});
            skLineSegment(sketch, "E412", {"start": v(-8.04, 6.98) * mm, "end": v(-8, 6.9) * mm});
            skLineSegment(sketch, "E413", {"start": v(-8, 6.9) * mm, "end": v(-7.97, 6.83) * mm});
            skLineSegment(sketch, "E414", {"start": v(-7.97, 6.83) * mm, "end": v(-7.94, 6.75) * mm});
            skLineSegment(sketch, "E415", {"start": v(-7.94, 6.75) * mm, "end": v(-7.9, 6.68) * mm});
            skLineSegment(sketch, "E416", {"start": v(-7.9, 6.68) * mm, "end": v(-7.88, 6.62) * mm});
            skLineSegment(sketch, "E417", {"start": v(-7.88, 6.62) * mm, "end": v(-7.84, 6.55) * mm});
            skLineSegment(sketch, "E418", {"start": v(-7.84, 6.55) * mm, "end": v(-7.81, 6.5) * mm});
            skLineSegment(sketch, "E419", {"start": v(-7.81, 6.5) * mm, "end": v(-7.78, 6.43) * mm});
            skLineSegment(sketch, "E420", {"start": v(-7.78, 6.43) * mm, "end": v(-7.75, 6.38) * mm});
            skLineSegment(sketch, "E421", {"start": v(-7.75, 6.38) * mm, "end": v(-7.72, 6.33) * mm});
            skLineSegment(sketch, "E422", {"start": v(-7.72, 6.33) * mm, "end": v(-7.69, 6.28) * mm});
            skLineSegment(sketch, "E423", {"start": v(-7.69, 6.28) * mm, "end": v(-7.66, 6.23) * mm});
            skLineSegment(sketch, "E424", {"start": v(-7.66, 6.23) * mm, "end": v(-7.62, 6.17) * mm});
            skLineSegment(sketch, "E425", {"start": v(-7.62, 6.17) * mm, "end": v(-7.58, 6.11) * mm});
            skLineSegment(sketch, "E426", {"start": v(-7.58, 6.11) * mm, "end": v(-7.54, 6.06) * mm});
            skLineSegment(sketch, "E427", {"start": v(-7.54, 6.06) * mm, "end": v(-7.5, 6.02) * mm});
            skLineSegment(sketch, "E428", {"start": v(-7.5, 6.02) * mm, "end": v(-7.46, 5.96) * mm});
            skLineSegment(sketch, "E429", {"start": v(-7.46, 5.96) * mm, "end": v(-7.43, 5.92) * mm});
            skLineSegment(sketch, "E430", {"start": v(-7.43, 5.92) * mm, "end": v(-7.39, 5.89) * mm});
            skLineSegment(sketch, "E431", {"start": v(-7.39, 5.89) * mm, "end": v(-7.35, 5.85) * mm});
            skLineSegment(sketch, "E432", {"start": v(-7.35, 5.85) * mm, "end": v(-6.6, 5.25) * mm});
            skArc(sketch, "E433", {"start": v(-6.6, 5.25) * mm, "mid": v(-7, 4.67) * mm, "end": v(-7.38, 4.09) * mm});
            skLineSegment(sketch, "E434", {"start": v(-7.38, 4.09) * mm, "end": v(-8.22, 4.55) * mm});
            skLineSegment(sketch, "E435", {"start": v(-8.22, 4.55) * mm, "end": v(-8.27, 4.57) * mm});
            skLineSegment(sketch, "E436", {"start": v(-8.27, 4.57) * mm, "end": v(-8.32, 4.6) * mm});
            skLineSegment(sketch, "E437", {"start": v(-8.32, 4.6) * mm, "end": v(-8.37, 4.61) * mm});
            skLineSegment(sketch, "E438", {"start": v(-8.37, 4.61) * mm, "end": v(-8.43, 4.63) * mm});
            skLineSegment(sketch, "E439", {"start": v(-8.43, 4.63) * mm, "end": v(-8.48, 4.65) * mm});
            skLineSegment(sketch, "E440", {"start": v(-8.48, 4.65) * mm, "end": v(-8.55, 4.66) * mm});
            skLineSegment(sketch, "E441", {"start": v(-8.55, 4.66) * mm, "end": v(-8.61, 4.68) * mm});
            skLineSegment(sketch, "E442", {"start": v(-8.61, 4.68) * mm, "end": v(-8.69, 4.7) * mm});
            skLineSegment(sketch, "E443", {"start": v(-8.69, 4.7) * mm, "end": v(-8.74, 4.7) * mm});
            skLineSegment(sketch, "E444", {"start": v(-8.74, 4.7) * mm, "end": v(-8.8, 4.71) * mm});
            skLineSegment(sketch, "E445", {"start": v(-8.8, 4.71) * mm, "end": v(-8.86, 4.72) * mm});
            skLineSegment(sketch, "E446", {"start": v(-8.86, 4.72) * mm, "end": v(-8.92, 4.73) * mm});
            skLineSegment(sketch, "E447", {"start": v(-8.92, 4.73) * mm, "end": v(-8.99, 4.73) * mm});
            skLineSegment(sketch, "E448", {"start": v(-8.99, 4.73) * mm, "end": v(-9.05, 4.74) * mm});
            skLineSegment(sketch, "E449", {"start": v(-9.05, 4.74) * mm, "end": v(-9.13, 4.74) * mm});
            skLineSegment(sketch, "E450", {"start": v(-9.13, 4.74) * mm, "end": v(-9.2, 4.75) * mm});
            skLineSegment(sketch, "E451", {"start": v(-9.2, 4.75) * mm, "end": v(-9.28, 4.75) * mm});
            skLineSegment(sketch, "E452", {"start": v(-9.28, 4.75) * mm, "end": v(-9.36, 4.75) * mm});
            skLineSegment(sketch, "E453", {"start": v(-9.36, 4.75) * mm, "end": v(-9.44, 4.75) * mm});
            skLineSegment(sketch, "E454", {"start": v(-9.44, 4.75) * mm, "end": v(-9.53, 4.75) * mm});
            skLineSegment(sketch, "E455", {"start": v(-9.53, 4.75) * mm, "end": v(-9.62, 4.75) * mm});
            skLineSegment(sketch, "E456", {"start": v(-9.62, 4.75) * mm, "end": v(-9.7, 4.74) * mm});
            skLineSegment(sketch, "E457", {"start": v(-9.7, 4.74) * mm, "end": v(-9.8, 4.74) * mm});
            skLineSegment(sketch, "E458", {"start": v(-9.8, 4.74) * mm, "end": v(-9.9, 4.73) * mm});
            skLineSegment(sketch, "E459", {"start": v(-9.9, 4.73) * mm, "end": v(-10, 4.72) * mm});
            skLineSegment(sketch, "E460", {"start": v(-10, 4.72) * mm, "end": v(-10.05, 4.71) * mm});
            skLineSegment(sketch, "E461", {"start": v(-10.05, 4.71) * mm, "end": v(-10.1, 4.7) * mm});
            skLineSegment(sketch, "E462", {"start": v(-10.1, 4.7) * mm, "end": v(-10.15, 4.7) * mm});
            skLineSegment(sketch, "E463", {"start": v(-10.15, 4.7) * mm, "end": v(-10.23, 4.69) * mm});
            skLineSegment(sketch, "E464", {"start": v(-10.23, 4.69) * mm, "end": v(-10.55, 3.92) * mm});
            skLineSegment(sketch, "E465", {"start": v(-10.55, 3.92) * mm, "end": v(-10.5, 3.86) * mm});
            skLineSegment(sketch, "E466", {"start": v(-10.5, 3.86) * mm, "end": v(-10.47, 3.81) * mm});
            skLineSegment(sketch, "E467", {"start": v(-10.47, 3.81) * mm, "end": v(-10.44, 3.77) * mm});
            skLineSegment(sketch, "E468", {"start": v(-10.44, 3.77) * mm, "end": v(-10.4, 3.73) * mm});
            skLineSegment(sketch, "E469", {"start": v(-10.4, 3.73) * mm, "end": v(-10.34, 3.66) * mm});
            skLineSegment(sketch, "E470", {"start": v(-10.34, 3.66) * mm, "end": v(-10.28, 3.58) * mm});
            skLineSegment(sketch, "E471", {"start": v(-10.28, 3.58) * mm, "end": v(-10.22, 3.5) * mm});
            skLineSegment(sketch, "E472", {"start": v(-10.22, 3.5) * mm, "end": v(-10.16, 3.44) * mm});
            skLineSegment(sketch, "E473", {"start": v(-10.16, 3.44) * mm, "end": v(-10.1, 3.38) * mm});
            skLineSegment(sketch, "E474", {"start": v(-10.1, 3.38) * mm, "end": v(-10.04, 3.31) * mm});
            skLineSegment(sketch, "E475", {"start": v(-10.04, 3.31) * mm, "end": v(-9.98, 3.26) * mm});
            skLineSegment(sketch, "E476", {"start": v(-9.98, 3.26) * mm, "end": v(-9.92, 3.2) * mm});
            skLineSegment(sketch, "E477", {"start": v(-9.92, 3.2) * mm, "end": v(-9.86, 3.15) * mm});
            skLineSegment(sketch, "E478", {"start": v(-9.86, 3.15) * mm, "end": v(-9.8, 3.1) * mm});
            skLineSegment(sketch, "E479", {"start": v(-9.8, 3.1) * mm, "end": v(-9.75, 3.05) * mm});
            skLineSegment(sketch, "E480", {"start": v(-9.75, 3.05) * mm, "end": v(-9.7, 3) * mm});
            skLineSegment(sketch, "E481", {"start": v(-9.7, 3) * mm, "end": v(-9.65, 2.97) * mm});
            skLineSegment(sketch, "E482", {"start": v(-9.65, 2.97) * mm, "end": v(-9.6, 2.93) * mm});
            skLineSegment(sketch, "E483", {"start": v(-9.6, 2.93) * mm, "end": v(-9.55, 2.9) * mm});
            skLineSegment(sketch, "E484", {"start": v(-9.55, 2.9) * mm, "end": v(-9.5, 2.86) * mm});
            skLineSegment(sketch, "E485", {"start": v(-9.5, 2.86) * mm, "end": v(-9.46, 2.83) * mm});
            skLineSegment(sketch, "E486", {"start": v(-9.46, 2.83) * mm, "end": v(-9.4, 2.78) * mm});
            skLineSegment(sketch, "E487", {"start": v(-9.4, 2.78) * mm, "end": v(-9.34, 2.75) * mm});
            skLineSegment(sketch, "E488", {"start": v(-9.34, 2.75) * mm, "end": v(-9.29, 2.71) * mm});
            skLineSegment(sketch, "E489", {"start": v(-9.29, 2.71) * mm, "end": v(-9.24, 2.69) * mm});
            skLineSegment(sketch, "E490", {"start": v(-9.24, 2.69) * mm, "end": v(-9.18, 2.65) * mm});
            skLineSegment(sketch, "E491", {"start": v(-9.18, 2.65) * mm, "end": v(-9.13, 2.63) * mm});
            skLineSegment(sketch, "E492", {"start": v(-9.13, 2.63) * mm, "end": v(-9.08, 2.61) * mm});
            skLineSegment(sketch, "E493", {"start": v(-9.08, 2.61) * mm, "end": v(-9.03, 2.6) * mm});
            skLineSegment(sketch, "E494", {"start": v(-9.03, 2.6) * mm, "end": v(-8.1, 2.33) * mm});
            skArc(sketch, "E495", {"start": v(-8.1, 2.33) * mm, "mid": v(-8.25, 1.64) * mm, "end": v(-8.38, 0.95) * mm});
            skLineSegment(sketch, "E496", {"start": v(-8.38, 0.95) * mm, "end": v(-9.34, 1.06) * mm});
            skLineSegment(sketch, "E497", {"start": v(-9.34, 1.06) * mm, "end": v(-9.39, 1.06) * mm});
            skLineSegment(sketch, "E498", {"start": v(-9.39, 1.06) * mm, "end": v(-9.44, 1.06) * mm});
            skLineSegment(sketch, "E499", {"start": v(-9.44, 1.06) * mm, "end": v(-9.5, 1.06) * mm});
            skLineSegment(sketch, "E500", {"start": v(-9.5, 1.06) * mm, "end": v(-9.56, 1.05) * mm});
            skLineSegment(sketch, "E501", {"start": v(-9.56, 1.05) * mm, "end": v(-9.62, 1.05) * mm});
            skLineSegment(sketch, "E502", {"start": v(-9.62, 1.05) * mm, "end": v(-9.68, 1.04) * mm});
            skLineSegment(sketch, "E503", {"start": v(-9.68, 1.04) * mm, "end": v(-9.75, 1.03) * mm});
            skLineSegment(sketch, "E504", {"start": v(-9.75, 1.03) * mm, "end": v(-9.82, 1.01) * mm});
            skLineSegment(sketch, "E505", {"start": v(-9.82, 1.01) * mm, "end": v(-9.88, 1) * mm});
            skLineSegment(sketch, "E506", {"start": v(-9.88, 1) * mm, "end": v(-9.93, 0.99) * mm});
            skLineSegment(sketch, "E507", {"start": v(-9.93, 0.99) * mm, "end": v(-9.99, 0.97) * mm});
            skLineSegment(sketch, "E508", {"start": v(-9.99, 0.97) * mm, "end": v(-10.05, 0.95) * mm});
            skLineSegment(sketch, "E509", {"start": v(-10.05, 0.95) * mm, "end": v(-10.11, 0.93) * mm});
            skLineSegment(sketch, "E510", {"start": v(-10.11, 0.93) * mm, "end": v(-10.18, 0.91) * mm});
            skLineSegment(sketch, "E511", {"start": v(-10.18, 0.91) * mm, "end": v(-10.25, 0.9) * mm});
            skLineSegment(sketch, "E512", {"start": v(-10.25, 0.9) * mm, "end": v(-10.32, 0.87) * mm});
            skLineSegment(sketch, "E513", {"start": v(-10.32, 0.87) * mm, "end": v(-10.39, 0.84) * mm});
            skLineSegment(sketch, "E514", {"start": v(-10.39, 0.84) * mm, "end": v(-10.46, 0.8) * mm});
            skLineSegment(sketch, "E515", {"start": v(-10.46, 0.8) * mm, "end": v(-10.54, 0.78) * mm});
            skLineSegment(sketch, "E516", {"start": v(-10.54, 0.78) * mm, "end": v(-10.62, 0.74) * mm});
            skLineSegment(sketch, "E517", {"start": v(-10.62, 0.74) * mm, "end": v(-10.7, 0.7) * mm});
            skLineSegment(sketch, "E518", {"start": v(-10.7, 0.7) * mm, "end": v(-10.78, 0.67) * mm});
            skLineSegment(sketch, "E519", {"start": v(-10.78, 0.67) * mm, "end": v(-10.87, 0.63) * mm});
            skLineSegment(sketch, "E520", {"start": v(-10.87, 0.63) * mm, "end": v(-10.95, 0.58) * mm});
            skLineSegment(sketch, "E521", {"start": v(-10.95, 0.58) * mm, "end": v(-11.04, 0.53) * mm});
            skLineSegment(sketch, "E522", {"start": v(-11.04, 0.53) * mm, "end": v(-11.09, 0.5) * mm});
            skLineSegment(sketch, "E523", {"start": v(-11.09, 0.5) * mm, "end": v(-11.13, 0.48) * mm});
            skLineSegment(sketch, "E524", {"start": v(-11.13, 0.48) * mm, "end": v(-11.18, 0.46) * mm});
            skLineSegment(sketch, "E525", {"start": v(-11.18, 0.46) * mm, "end": v(-11.24, 0.42) * mm});
            skLineSegment(sketch, "E526", {"start": v(-11.24, 0.42) * mm, "end": v(-11.24, -0.42) * mm});
            skLineSegment(sketch, "E527", {"start": v(-11.24, -0.42) * mm, "end": v(-11.18, -0.46) * mm});
            skLineSegment(sketch, "E528", {"start": v(-11.18, -0.46) * mm, "end": v(-11.13, -0.48) * mm});
            skLineSegment(sketch, "E529", {"start": v(-11.13, -0.48) * mm, "end": v(-11.09, -0.5) * mm});
            skLineSegment(sketch, "E530", {"start": v(-11.09, -0.5) * mm, "end": v(-11.04, -0.53) * mm});
            skLineSegment(sketch, "E531", {"start": v(-11.04, -0.53) * mm, "end": v(-10.95, -0.58) * mm});
            skLineSegment(sketch, "E532", {"start": v(-10.95, -0.58) * mm, "end": v(-10.87, -0.63) * mm});
            skLineSegment(sketch, "E533", {"start": v(-10.87, -0.63) * mm, "end": v(-10.78, -0.67) * mm});
            skLineSegment(sketch, "E534", {"start": v(-10.78, -0.67) * mm, "end": v(-10.7, -0.7) * mm});
            skLineSegment(sketch, "E535", {"start": v(-10.7, -0.7) * mm, "end": v(-10.62, -0.74) * mm});
            skLineSegment(sketch, "E536", {"start": v(-10.62, -0.74) * mm, "end": v(-10.54, -0.78) * mm});
            skLineSegment(sketch, "E537", {"start": v(-10.54, -0.78) * mm, "end": v(-10.46, -0.8) * mm});
            skLineSegment(sketch, "E538", {"start": v(-10.46, -0.8) * mm, "end": v(-10.39, -0.84) * mm});
            skLineSegment(sketch, "E539", {"start": v(-10.39, -0.84) * mm, "end": v(-10.32, -0.87) * mm});
            skLineSegment(sketch, "E540", {"start": v(-10.32, -0.87) * mm, "end": v(-10.25, -0.9) * mm});
            skLineSegment(sketch, "E541", {"start": v(-10.25, -0.9) * mm, "end": v(-10.18, -0.91) * mm});
            skLineSegment(sketch, "E542", {"start": v(-10.18, -0.91) * mm, "end": v(-10.11, -0.93) * mm});
            skLineSegment(sketch, "E543", {"start": v(-10.11, -0.93) * mm, "end": v(-10.05, -0.95) * mm});
            skLineSegment(sketch, "E544", {"start": v(-10.05, -0.95) * mm, "end": v(-9.99, -0.97) * mm});
            skLineSegment(sketch, "E545", {"start": v(-9.99, -0.97) * mm, "end": v(-9.93, -0.99) * mm});
            skLineSegment(sketch, "E546", {"start": v(-9.93, -0.99) * mm, "end": v(-9.88, -1) * mm});
            skLineSegment(sketch, "E547", {"start": v(-9.88, -1) * mm, "end": v(-9.82, -1.01) * mm});
            skLineSegment(sketch, "E548", {"start": v(-9.82, -1.01) * mm, "end": v(-9.75, -1.03) * mm});
            skLineSegment(sketch, "E549", {"start": v(-9.75, -1.03) * mm, "end": v(-9.68, -1.04) * mm});
            skLineSegment(sketch, "E550", {"start": v(-9.68, -1.04) * mm, "end": v(-9.62, -1.05) * mm});
            skLineSegment(sketch, "E551", {"start": v(-9.62, -1.05) * mm, "end": v(-9.56, -1.05) * mm});
            skLineSegment(sketch, "E552", {"start": v(-9.56, -1.05) * mm, "end": v(-9.5, -1.06) * mm});
            skLineSegment(sketch, "E553", {"start": v(-9.5, -1.06) * mm, "end": v(-9.44, -1.06) * mm});
            skLineSegment(sketch, "E554", {"start": v(-9.44, -1.06) * mm, "end": v(-9.39, -1.06) * mm});
            skLineSegment(sketch, "E555", {"start": v(-9.39, -1.06) * mm, "end": v(-9.34, -1.06) * mm});
            skLineSegment(sketch, "E556", {"start": v(-9.34, -1.06) * mm, "end": v(-8.38, -0.95) * mm});
            skArc(sketch, "E557", {"start": v(-8.38, -0.95) * mm, "mid": v(-8.25, -1.64) * mm, "end": v(-8.1, -2.33) * mm});
            skLineSegment(sketch, "E558", {"start": v(-8.1, -2.33) * mm, "end": v(-9.03, -2.6) * mm});
            skLineSegment(sketch, "E559", {"start": v(-9.03, -2.6) * mm, "end": v(-9.08, -2.61) * mm});
            skLineSegment(sketch, "E560", {"start": v(-9.08, -2.61) * mm, "end": v(-9.13, -2.63) * mm});
            skLineSegment(sketch, "E561", {"start": v(-9.13, -2.63) * mm, "end": v(-9.18, -2.65) * mm});
            skLineSegment(sketch, "E562", {"start": v(-9.18, -2.65) * mm, "end": v(-9.24, -2.69) * mm});
            skLineSegment(sketch, "E563", {"start": v(-9.24, -2.69) * mm, "end": v(-9.29, -2.71) * mm});
            skLineSegment(sketch, "E564", {"start": v(-9.29, -2.71) * mm, "end": v(-9.34, -2.75) * mm});
            skLineSegment(sketch, "E565", {"start": v(-9.34, -2.75) * mm, "end": v(-9.4, -2.78) * mm});
            skLineSegment(sketch, "E566", {"start": v(-9.4, -2.78) * mm, "end": v(-9.46, -2.83) * mm});
            skLineSegment(sketch, "E567", {"start": v(-9.46, -2.83) * mm, "end": v(-9.5, -2.86) * mm});
            skLineSegment(sketch, "E568", {"start": v(-9.5, -2.86) * mm, "end": v(-9.55, -2.9) * mm});
            skLineSegment(sketch, "E569", {"start": v(-9.55, -2.9) * mm, "end": v(-9.6, -2.93) * mm});
            skLineSegment(sketch, "E570", {"start": v(-9.6, -2.93) * mm, "end": v(-9.65, -2.97) * mm});
            skLineSegment(sketch, "E571", {"start": v(-9.65, -2.97) * mm, "end": v(-9.7, -3) * mm});
            skLineSegment(sketch, "E572", {"start": v(-9.7, -3) * mm, "end": v(-9.75, -3.05) * mm});
            skLineSegment(sketch, "E573", {"start": v(-9.75, -3.05) * mm, "end": v(-9.8, -3.1) * mm});
            skLineSegment(sketch, "E574", {"start": v(-9.8, -3.1) * mm, "end": v(-9.86, -3.15) * mm});
            skLineSegment(sketch, "E575", {"start": v(-9.86, -3.15) * mm, "end": v(-9.92, -3.2) * mm});
            skLineSegment(sketch, "E576", {"start": v(-9.92, -3.2) * mm, "end": v(-9.98, -3.26) * mm});
            skLineSegment(sketch, "E577", {"start": v(-9.98, -3.26) * mm, "end": v(-10.04, -3.31) * mm});
            skLineSegment(sketch, "E578", {"start": v(-10.04, -3.31) * mm, "end": v(-10.1, -3.38) * mm});
            skLineSegment(sketch, "E579", {"start": v(-10.1, -3.38) * mm, "end": v(-10.16, -3.44) * mm});
            skLineSegment(sketch, "E580", {"start": v(-10.16, -3.44) * mm, "end": v(-10.22, -3.5) * mm});
            skLineSegment(sketch, "E581", {"start": v(-10.22, -3.5) * mm, "end": v(-10.28, -3.58) * mm});
            skLineSegment(sketch, "E582", {"start": v(-10.28, -3.58) * mm, "end": v(-10.34, -3.66) * mm});
            skLineSegment(sketch, "E583", {"start": v(-10.34, -3.66) * mm, "end": v(-10.4, -3.73) * mm});
            skLineSegment(sketch, "E584", {"start": v(-10.4, -3.73) * mm, "end": v(-10.44, -3.77) * mm});
            skLineSegment(sketch, "E585", {"start": v(-10.44, -3.77) * mm, "end": v(-10.47, -3.81) * mm});
            skLineSegment(sketch, "E586", {"start": v(-10.47, -3.81) * mm, "end": v(-10.5, -3.86) * mm});
            skLineSegment(sketch, "E587", {"start": v(-10.5, -3.86) * mm, "end": v(-10.55, -3.92) * mm});
            skLineSegment(sketch, "E588", {"start": v(-10.55, -3.92) * mm, "end": v(-10.23, -4.69) * mm});
            skLineSegment(sketch, "E589", {"start": v(-10.23, -4.69) * mm, "end": v(-10.15, -4.7) * mm});
            skLineSegment(sketch, "E590", {"start": v(-10.15, -4.7) * mm, "end": v(-10.1, -4.7) * mm});
            skLineSegment(sketch, "E591", {"start": v(-10.1, -4.7) * mm, "end": v(-10.05, -4.71) * mm});
            skLineSegment(sketch, "E592", {"start": v(-10.05, -4.71) * mm, "end": v(-10, -4.72) * mm});
            skLineSegment(sketch, "E593", {"start": v(-10, -4.72) * mm, "end": v(-9.9, -4.73) * mm});
            skLineSegment(sketch, "E594", {"start": v(-9.9, -4.73) * mm, "end": v(-9.8, -4.74) * mm});
            skLineSegment(sketch, "E595", {"start": v(-9.8, -4.74) * mm, "end": v(-9.7, -4.74) * mm});
            skLineSegment(sketch, "E596", {"start": v(-9.7, -4.74) * mm, "end": v(-9.62, -4.75) * mm});
            skLineSegment(sketch, "E597", {"start": v(-9.62, -4.75) * mm, "end": v(-9.53, -4.75) * mm});
            skLineSegment(sketch, "E598", {"start": v(-9.53, -4.75) * mm, "end": v(-9.44, -4.75) * mm});
            skLineSegment(sketch, "E599", {"start": v(-9.44, -4.75) * mm, "end": v(-9.36, -4.75) * mm});
            skLineSegment(sketch, "E600", {"start": v(-9.36, -4.75) * mm, "end": v(-9.28, -4.75) * mm});
            skLineSegment(sketch, "E601", {"start": v(-9.28, -4.75) * mm, "end": v(-9.2, -4.75) * mm});
            skLineSegment(sketch, "E602", {"start": v(-9.2, -4.75) * mm, "end": v(-9.13, -4.74) * mm});
            skLineSegment(sketch, "E603", {"start": v(-9.13, -4.74) * mm, "end": v(-9.05, -4.74) * mm});
            skLineSegment(sketch, "E604", {"start": v(-9.05, -4.74) * mm, "end": v(-8.99, -4.73) * mm});
            skLineSegment(sketch, "E605", {"start": v(-8.99, -4.73) * mm, "end": v(-8.92, -4.73) * mm});
            skLineSegment(sketch, "E606", {"start": v(-8.92, -4.73) * mm, "end": v(-8.86, -4.72) * mm});
            skLineSegment(sketch, "E607", {"start": v(-8.86, -4.72) * mm, "end": v(-8.8, -4.71) * mm});
            skLineSegment(sketch, "E608", {"start": v(-8.8, -4.71) * mm, "end": v(-8.74, -4.7) * mm});
            skLineSegment(sketch, "E609", {"start": v(-8.74, -4.7) * mm, "end": v(-8.69, -4.7) * mm});
            skLineSegment(sketch, "E610", {"start": v(-8.69, -4.7) * mm, "end": v(-8.61, -4.68) * mm});
            skLineSegment(sketch, "E611", {"start": v(-8.61, -4.68) * mm, "end": v(-8.55, -4.66) * mm});
            skLineSegment(sketch, "E612", {"start": v(-8.55, -4.66) * mm, "end": v(-8.48, -4.65) * mm});
            skLineSegment(sketch, "E613", {"start": v(-8.48, -4.65) * mm, "end": v(-8.43, -4.63) * mm});
            skLineSegment(sketch, "E614", {"start": v(-8.43, -4.63) * mm, "end": v(-8.37, -4.61) * mm});
            skLineSegment(sketch, "E615", {"start": v(-8.37, -4.61) * mm, "end": v(-8.32, -4.6) * mm});
            skLineSegment(sketch, "E616", {"start": v(-8.32, -4.6) * mm, "end": v(-8.27, -4.57) * mm});
            skLineSegment(sketch, "E617", {"start": v(-8.27, -4.57) * mm, "end": v(-8.22, -4.55) * mm});
            skLineSegment(sketch, "E618", {"start": v(-8.22, -4.55) * mm, "end": v(-7.38, -4.09) * mm});
            skArc(sketch, "E619", {"start": v(-7.38, -4.09) * mm, "mid": v(-7, -4.67) * mm, "end": v(-6.6, -5.25) * mm});
            skLineSegment(sketch, "E620", {"start": v(-6.6, -5.25) * mm, "end": v(-7.35, -5.85) * mm});
            skLineSegment(sketch, "E621", {"start": v(-7.35, -5.85) * mm, "end": v(-7.4, -5.89) * mm});
            skLineSegment(sketch, "E622", {"start": v(-7.4, -5.89) * mm, "end": v(-7.43, -5.92) * mm});
            skLineSegment(sketch, "E623", {"start": v(-7.43, -5.92) * mm, "end": v(-7.46, -5.96) * mm});
            skLineSegment(sketch, "E624", {"start": v(-7.46, -5.96) * mm, "end": v(-7.5, -6.02) * mm});
            skLineSegment(sketch, "E625", {"start": v(-7.5, -6.02) * mm, "end": v(-7.54, -6.06) * mm});
            skLineSegment(sketch, "E626", {"start": v(-7.54, -6.06) * mm, "end": v(-7.58, -6.11) * mm});
            skLineSegment(sketch, "E627", {"start": v(-7.58, -6.11) * mm, "end": v(-7.62, -6.17) * mm});
            skLineSegment(sketch, "E628", {"start": v(-7.62, -6.17) * mm, "end": v(-7.66, -6.23) * mm});
            skLineSegment(sketch, "E629", {"start": v(-7.66, -6.23) * mm, "end": v(-7.69, -6.28) * mm});
            skLineSegment(sketch, "E630", {"start": v(-7.69, -6.28) * mm, "end": v(-7.72, -6.33) * mm});
            skLineSegment(sketch, "E631", {"start": v(-7.72, -6.33) * mm, "end": v(-7.75, -6.38) * mm});
            skLineSegment(sketch, "E632", {"start": v(-7.75, -6.38) * mm, "end": v(-7.78, -6.43) * mm});
            skLineSegment(sketch, "E633", {"start": v(-7.78, -6.43) * mm, "end": v(-7.81, -6.5) * mm});
            skLineSegment(sketch, "E634", {"start": v(-7.81, -6.5) * mm, "end": v(-7.84, -6.55) * mm});
            skLineSegment(sketch, "E635", {"start": v(-7.84, -6.55) * mm, "end": v(-7.88, -6.62) * mm});
            skLineSegment(sketch, "E636", {"start": v(-7.88, -6.62) * mm, "end": v(-7.9, -6.68) * mm});
            skLineSegment(sketch, "E637", {"start": v(-7.9, -6.68) * mm, "end": v(-7.94, -6.75) * mm});
            skLineSegment(sketch, "E638", {"start": v(-7.94, -6.75) * mm, "end": v(-7.97, -6.83) * mm});
            skLineSegment(sketch, "E639", {"start": v(-7.97, -6.83) * mm, "end": v(-8, -6.9) * mm});
            skLineSegment(sketch, "E640", {"start": v(-8, -6.9) * mm, "end": v(-8.04, -6.98) * mm});
            skLineSegment(sketch, "E641", {"start": v(-8.04, -6.98) * mm, "end": v(-8.07, -7.07) * mm});
            skLineSegment(sketch, "E642", {"start": v(-8.07, -7.07) * mm, "end": v(-8.1, -7.15) * mm});
            skLineSegment(sketch, "E643", {"start": v(-8.1, -7.15) * mm, "end": v(-8.13, -7.24) * mm});
            skLineSegment(sketch, "E644", {"start": v(-8.13, -7.24) * mm, "end": v(-8.16, -7.33) * mm});
            skLineSegment(sketch, "E645", {"start": v(-8.16, -7.33) * mm, "end": v(-8.18, -7.43) * mm});
            skLineSegment(sketch, "E646", {"start": v(-8.18, -7.43) * mm, "end": v(-8.2, -7.48) * mm});
            skLineSegment(sketch, "E647", {"start": v(-8.2, -7.48) * mm, "end": v(-8.21, -7.53) * mm});
            skLineSegment(sketch, "E648", {"start": v(-8.21, -7.53) * mm, "end": v(-8.23, -7.58) * mm});
            skLineSegment(sketch, "E649", {"start": v(-8.23, -7.58) * mm, "end": v(-8.24, -7.66) * mm});
            skLineSegment(sketch, "E650", {"start": v(-8.24, -7.66) * mm, "end": v(-7.66, -8.24) * mm});
            skLineSegment(sketch, "E651", {"start": v(-7.66, -8.24) * mm, "end": v(-7.58, -8.23) * mm});
            skLineSegment(sketch, "E652", {"start": v(-7.58, -8.23) * mm, "end": v(-7.53, -8.21) * mm});
            skLineSegment(sketch, "E653", {"start": v(-7.53, -8.21) * mm, "end": v(-7.48, -8.2) * mm});
            skLineSegment(sketch, "E654", {"start": v(-7.48, -8.2) * mm, "end": v(-7.43, -8.18) * mm});
            skLineSegment(sketch, "E655", {"start": v(-7.43, -8.18) * mm, "end": v(-7.33, -8.16) * mm});
            skLineSegment(sketch, "E656", {"start": v(-7.33, -8.16) * mm, "end": v(-7.24, -8.13) * mm});
            skLineSegment(sketch, "E657", {"start": v(-7.24, -8.13) * mm, "end": v(-7.15, -8.1) * mm});
            skLineSegment(sketch, "E658", {"start": v(-7.15, -8.1) * mm, "end": v(-7.07, -8.07) * mm});
            skLineSegment(sketch, "E659", {"start": v(-7.07, -8.07) * mm, "end": v(-6.98, -8.04) * mm});
            skLineSegment(sketch, "E660", {"start": v(-6.98, -8.04) * mm, "end": v(-6.9, -8) * mm});
            skLineSegment(sketch, "E661", {"start": v(-6.9, -8) * mm, "end": v(-6.83, -7.97) * mm});
            skLineSegment(sketch, "E662", {"start": v(-6.83, -7.97) * mm, "end": v(-6.75, -7.94) * mm});
            skLineSegment(sketch, "E663", {"start": v(-6.75, -7.94) * mm, "end": v(-6.68, -7.9) * mm});
            skLineSegment(sketch, "E664", {"start": v(-6.68, -7.9) * mm, "end": v(-6.62, -7.88) * mm});
            skLineSegment(sketch, "E665", {"start": v(-6.62, -7.88) * mm, "end": v(-6.55, -7.84) * mm});
            skLineSegment(sketch, "E666", {"start": v(-6.55, -7.84) * mm, "end": v(-6.5, -7.81) * mm});
            skLineSegment(sketch, "E667", {"start": v(-6.5, -7.81) * mm, "end": v(-6.43, -7.78) * mm});
            skLineSegment(sketch, "E668", {"start": v(-6.43, -7.78) * mm, "end": v(-6.38, -7.75) * mm});
            skLineSegment(sketch, "E669", {"start": v(-6.38, -7.75) * mm, "end": v(-6.33, -7.72) * mm});
            skLineSegment(sketch, "E670", {"start": v(-6.33, -7.72) * mm, "end": v(-6.28, -7.69) * mm});
            skLineSegment(sketch, "E671", {"start": v(-6.28, -7.69) * mm, "end": v(-6.23, -7.66) * mm});
            skLineSegment(sketch, "E672", {"start": v(-6.23, -7.66) * mm, "end": v(-6.17, -7.62) * mm});
            skLineSegment(sketch, "E673", {"start": v(-6.17, -7.62) * mm, "end": v(-6.11, -7.58) * mm});
            skLineSegment(sketch, "E674", {"start": v(-6.11, -7.58) * mm, "end": v(-6.06, -7.54) * mm});
            skLineSegment(sketch, "E675", {"start": v(-6.06, -7.54) * mm, "end": v(-6.02, -7.5) * mm});
            skLineSegment(sketch, "E676", {"start": v(-6.02, -7.5) * mm, "end": v(-5.96, -7.46) * mm});
            skLineSegment(sketch, "E677", {"start": v(-5.96, -7.46) * mm, "end": v(-5.92, -7.43) * mm});
            skLineSegment(sketch, "E678", {"start": v(-5.92, -7.43) * mm, "end": v(-5.89, -7.39) * mm});
            skLineSegment(sketch, "E679", {"start": v(-5.89, -7.39) * mm, "end": v(-5.85, -7.35) * mm});
            skLineSegment(sketch, "E680", {"start": v(-5.85, -7.35) * mm, "end": v(-5.25, -6.6) * mm});
            skArc(sketch, "E681", {"start": v(-5.25, -6.6) * mm, "mid": v(-4.67, -7) * mm, "end": v(-4.09, -7.38) * mm});
            skLineSegment(sketch, "E682", {"start": v(-4.09, -7.38) * mm, "end": v(-4.55, -8.22) * mm});
            skLineSegment(sketch, "E683", {"start": v(-4.55, -8.22) * mm, "end": v(-4.57, -8.27) * mm});
            skLineSegment(sketch, "E684", {"start": v(-4.57, -8.27) * mm, "end": v(-4.6, -8.32) * mm});
            skLineSegment(sketch, "E685", {"start": v(-4.6, -8.32) * mm, "end": v(-4.61, -8.37) * mm});
            skLineSegment(sketch, "E686", {"start": v(-4.61, -8.37) * mm, "end": v(-4.63, -8.43) * mm});
            skLineSegment(sketch, "E687", {"start": v(-4.63, -8.43) * mm, "end": v(-4.65, -8.48) * mm});
            skLineSegment(sketch, "E688", {"start": v(-4.65, -8.48) * mm, "end": v(-4.66, -8.55) * mm});
            skLineSegment(sketch, "E689", {"start": v(-4.66, -8.55) * mm, "end": v(-4.68, -8.61) * mm});
            skLineSegment(sketch, "E690", {"start": v(-4.68, -8.61) * mm, "end": v(-4.7, -8.69) * mm});
            skLineSegment(sketch, "E691", {"start": v(-4.7, -8.69) * mm, "end": v(-4.7, -8.74) * mm});
            skLineSegment(sketch, "E692", {"start": v(-4.7, -8.74) * mm, "end": v(-4.71, -8.8) * mm});
            skLineSegment(sketch, "E693", {"start": v(-4.71, -8.8) * mm, "end": v(-4.72, -8.86) * mm});
            skLineSegment(sketch, "E694", {"start": v(-4.72, -8.86) * mm, "end": v(-4.73, -8.92) * mm});
            skLineSegment(sketch, "E695", {"start": v(-4.73, -8.92) * mm, "end": v(-4.73, -8.99) * mm});
            skLineSegment(sketch, "E696", {"start": v(-4.73, -8.99) * mm, "end": v(-4.74, -9.05) * mm});
            skLineSegment(sketch, "E697", {"start": v(-4.74, -9.05) * mm, "end": v(-4.74, -9.13) * mm});
            skLineSegment(sketch, "E698", {"start": v(-4.74, -9.13) * mm, "end": v(-4.75, -9.2) * mm});
            skLineSegment(sketch, "E699", {"start": v(-4.75, -9.2) * mm, "end": v(-4.75, -9.28) * mm});
            skLineSegment(sketch, "E700", {"start": v(-4.75, -9.28) * mm, "end": v(-4.75, -9.36) * mm});
            skLineSegment(sketch, "E701", {"start": v(-4.75, -9.36) * mm, "end": v(-4.75, -9.44) * mm});
            skLineSegment(sketch, "E702", {"start": v(-4.75, -9.44) * mm, "end": v(-4.75, -9.53) * mm});
            skLineSegment(sketch, "E703", {"start": v(-4.75, -9.53) * mm, "end": v(-4.75, -9.62) * mm});
            skLineSegment(sketch, "E704", {"start": v(-4.75, -9.62) * mm, "end": v(-4.74, -9.7) * mm});
            skLineSegment(sketch, "E705", {"start": v(-4.74, -9.7) * mm, "end": v(-4.74, -9.8) * mm});
            skLineSegment(sketch, "E706", {"start": v(-4.74, -9.8) * mm, "end": v(-4.73, -9.9) * mm});
            skLineSegment(sketch, "E707", {"start": v(-4.73, -9.9) * mm, "end": v(-4.72, -10) * mm});
            skLineSegment(sketch, "E708", {"start": v(-4.72, -10) * mm, "end": v(-4.71, -10.05) * mm});
            skLineSegment(sketch, "E709", {"start": v(-4.71, -10.05) * mm, "end": v(-4.7, -10.1) * mm});
            skLineSegment(sketch, "E710", {"start": v(-4.7, -10.1) * mm, "end": v(-4.7, -10.15) * mm});
            skLineSegment(sketch, "E711", {"start": v(-4.7, -10.15) * mm, "end": v(-4.69, -10.23) * mm});
            skLineSegment(sketch, "E712", {"start": v(-4.69, -10.23) * mm, "end": v(-3.92, -10.55) * mm});
            skLineSegment(sketch, "E713", {"start": v(-3.92, -10.55) * mm, "end": v(-3.86, -10.5) * mm});
            skLineSegment(sketch, "E714", {"start": v(-3.86, -10.5) * mm, "end": v(-3.81, -10.47) * mm});
            skLineSegment(sketch, "E715", {"start": v(-3.81, -10.47) * mm, "end": v(-3.77, -10.44) * mm});
            skLineSegment(sketch, "E716", {"start": v(-3.77, -10.44) * mm, "end": v(-3.73, -10.4) * mm});
            skLineSegment(sketch, "E717", {"start": v(-3.73, -10.4) * mm, "end": v(-3.66, -10.34) * mm});
            skLineSegment(sketch, "E718", {"start": v(-3.66, -10.34) * mm, "end": v(-3.58, -10.28) * mm});
            skLineSegment(sketch, "E719", {"start": v(-3.58, -10.28) * mm, "end": v(-3.5, -10.22) * mm});
            skLineSegment(sketch, "E720", {"start": v(-3.5, -10.22) * mm, "end": v(-3.44, -10.16) * mm});
            skLineSegment(sketch, "E721", {"start": v(-3.44, -10.16) * mm, "end": v(-3.38, -10.1) * mm});
            skLineSegment(sketch, "E722", {"start": v(-3.38, -10.1) * mm, "end": v(-3.31, -10.04) * mm});
            skLineSegment(sketch, "E723", {"start": v(-3.31, -10.04) * mm, "end": v(-3.26, -9.98) * mm});
            skLineSegment(sketch, "E724", {"start": v(-3.26, -9.98) * mm, "end": v(-3.2, -9.92) * mm});
            skLineSegment(sketch, "E725", {"start": v(-3.2, -9.92) * mm, "end": v(-3.15, -9.86) * mm});
            skLineSegment(sketch, "E726", {"start": v(-3.15, -9.86) * mm, "end": v(-3.1, -9.8) * mm});
            skLineSegment(sketch, "E727", {"start": v(-3.1, -9.8) * mm, "end": v(-3.05, -9.75) * mm});
            skLineSegment(sketch, "E728", {"start": v(-3.05, -9.75) * mm, "end": v(-3, -9.7) * mm});
            skLineSegment(sketch, "E729", {"start": v(-3, -9.7) * mm, "end": v(-2.97, -9.65) * mm});
            skLineSegment(sketch, "E730", {"start": v(-2.97, -9.65) * mm, "end": v(-2.93, -9.6) * mm});
            skLineSegment(sketch, "E731", {"start": v(-2.93, -9.6) * mm, "end": v(-2.9, -9.55) * mm});
            skLineSegment(sketch, "E732", {"start": v(-2.9, -9.55) * mm, "end": v(-2.86, -9.5) * mm});
            skLineSegment(sketch, "E733", {"start": v(-2.86, -9.5) * mm, "end": v(-2.83, -9.46) * mm});
            skLineSegment(sketch, "E734", {"start": v(-2.83, -9.46) * mm, "end": v(-2.78, -9.4) * mm});
            skLineSegment(sketch, "E735", {"start": v(-2.78, -9.4) * mm, "end": v(-2.75, -9.34) * mm});
            skLineSegment(sketch, "E736", {"start": v(-2.75, -9.34) * mm, "end": v(-2.71, -9.29) * mm});
            skLineSegment(sketch, "E737", {"start": v(-2.71, -9.29) * mm, "end": v(-2.69, -9.24) * mm});
            skLineSegment(sketch, "E738", {"start": v(-2.69, -9.24) * mm, "end": v(-2.65, -9.18) * mm});
            skLineSegment(sketch, "E739", {"start": v(-2.65, -9.18) * mm, "end": v(-2.63, -9.13) * mm});
            skLineSegment(sketch, "E740", {"start": v(-2.63, -9.13) * mm, "end": v(-2.61, -9.08) * mm});
            skLineSegment(sketch, "E741", {"start": v(-2.61, -9.08) * mm, "end": v(-2.6, -9.03) * mm});
            skLineSegment(sketch, "E742", {"start": v(-2.6, -9.03) * mm, "end": v(-2.33, -8.1) * mm});
            skArc(sketch, "E743", {"start": v(-2.33, -8.1) * mm, "mid": v(-1.64, -8.25) * mm, "end": v(-0.95, -8.38) * mm});
            skLineSegment(sketch, "E744", {"start": v(-0.95, -8.38) * mm, "end": v(-1.06, -9.34) * mm});
            skLineSegment(sketch, "E745", {"start": v(-1.06, -9.34) * mm, "end": v(-1.06, -9.39) * mm});
            skLineSegment(sketch, "E746", {"start": v(-1.06, -9.39) * mm, "end": v(-1.06, -9.44) * mm});
            skLineSegment(sketch, "E747", {"start": v(-1.06, -9.44) * mm, "end": v(-1.06, -9.5) * mm});
            skLineSegment(sketch, "E748", {"start": v(-1.06, -9.5) * mm, "end": v(-1.05, -9.56) * mm});
            skLineSegment(sketch, "E749", {"start": v(-1.05, -9.56) * mm, "end": v(-1.05, -9.62) * mm});
            skLineSegment(sketch, "E750", {"start": v(-1.05, -9.62) * mm, "end": v(-1.04, -9.68) * mm});
            skLineSegment(sketch, "E751", {"start": v(-1.04, -9.68) * mm, "end": v(-1.03, -9.75) * mm});
            skLineSegment(sketch, "E752", {"start": v(-1.03, -9.75) * mm, "end": v(-1.01, -9.82) * mm});
            skLineSegment(sketch, "E753", {"start": v(-1.01, -9.82) * mm, "end": v(-1, -9.88) * mm});
            skLineSegment(sketch, "E754", {"start": v(-1, -9.88) * mm, "end": v(-0.99, -9.93) * mm});
            skLineSegment(sketch, "E755", {"start": v(-0.99, -9.93) * mm, "end": v(-0.97, -9.99) * mm});
            skLineSegment(sketch, "E756", {"start": v(-0.97, -9.99) * mm, "end": v(-0.95, -10.05) * mm});
            skLineSegment(sketch, "E757", {"start": v(-0.95, -10.05) * mm, "end": v(-0.93, -10.11) * mm});
            skLineSegment(sketch, "E758", {"start": v(-0.93, -10.11) * mm, "end": v(-0.91, -10.18) * mm});
            skLineSegment(sketch, "E759", {"start": v(-0.91, -10.18) * mm, "end": v(-0.9, -10.25) * mm});
            skLineSegment(sketch, "E760", {"start": v(-0.9, -10.25) * mm, "end": v(-0.87, -10.32) * mm});
            skLineSegment(sketch, "E761", {"start": v(-0.87, -10.32) * mm, "end": v(-0.84, -10.39) * mm});
            skLineSegment(sketch, "E762", {"start": v(-0.84, -10.39) * mm, "end": v(-0.8, -10.46) * mm});
            skLineSegment(sketch, "E763", {"start": v(-0.8, -10.46) * mm, "end": v(-0.78, -10.54) * mm});
            skLineSegment(sketch, "E764", {"start": v(-0.78, -10.54) * mm, "end": v(-0.74, -10.62) * mm});
            skLineSegment(sketch, "E765", {"start": v(-0.74, -10.62) * mm, "end": v(-0.7, -10.7) * mm});
            skLineSegment(sketch, "E766", {"start": v(-0.7, -10.7) * mm, "end": v(-0.67, -10.78) * mm});
            skLineSegment(sketch, "E767", {"start": v(-0.67, -10.78) * mm, "end": v(-0.63, -10.87) * mm});
            skLineSegment(sketch, "E768", {"start": v(-0.63, -10.87) * mm, "end": v(-0.58, -10.95) * mm});
            skLineSegment(sketch, "E769", {"start": v(-0.58, -10.95) * mm, "end": v(-0.53, -11.04) * mm});
            skLineSegment(sketch, "E770", {"start": v(-0.53, -11.04) * mm, "end": v(-0.5, -11.09) * mm});
            skLineSegment(sketch, "E771", {"start": v(-0.5, -11.09) * mm, "end": v(-0.48, -11.13) * mm});
            skLineSegment(sketch, "E772", {"start": v(-0.48, -11.13) * mm, "end": v(-0.46, -11.18) * mm});
            skLineSegment(sketch, "E773", {"start": v(-0.46, -11.18) * mm, "end": v(-0.42, -11.24) * mm});
            skLineSegment(sketch, "E774", {"start": v(-0.42, -11.24) * mm, "end": v(0.42, -11.24) * mm});
            skLineSegment(sketch, "E775", {"start": v(0.42, -11.24) * mm, "end": v(0.46, -11.18) * mm});
            skLineSegment(sketch, "E776", {"start": v(0.46, -11.18) * mm, "end": v(0.48, -11.13) * mm});
            skLineSegment(sketch, "E777", {"start": v(0.48, -11.13) * mm, "end": v(0.5, -11.09) * mm});
            skLineSegment(sketch, "E778", {"start": v(0.5, -11.09) * mm, "end": v(0.53, -11.04) * mm});
            skLineSegment(sketch, "E779", {"start": v(0.53, -11.04) * mm, "end": v(0.58, -10.95) * mm});
            skLineSegment(sketch, "E780", {"start": v(0.58, -10.95) * mm, "end": v(0.63, -10.87) * mm});
            skLineSegment(sketch, "E781", {"start": v(0.63, -10.87) * mm, "end": v(0.67, -10.78) * mm});
            skLineSegment(sketch, "E782", {"start": v(0.67, -10.78) * mm, "end": v(0.7, -10.7) * mm});
            skLineSegment(sketch, "E783", {"start": v(0.7, -10.7) * mm, "end": v(0.74, -10.62) * mm});
            skLineSegment(sketch, "E784", {"start": v(0.74, -10.62) * mm, "end": v(0.78, -10.54) * mm});
            skLineSegment(sketch, "E785", {"start": v(0.78, -10.54) * mm, "end": v(0.8, -10.46) * mm});
            skLineSegment(sketch, "E786", {"start": v(0.8, -10.46) * mm, "end": v(0.84, -10.39) * mm});
            skLineSegment(sketch, "E787", {"start": v(0.84, -10.39) * mm, "end": v(0.87, -10.32) * mm});
            skLineSegment(sketch, "E788", {"start": v(0.87, -10.32) * mm, "end": v(0.9, -10.25) * mm});
            skLineSegment(sketch, "E789", {"start": v(0.9, -10.25) * mm, "end": v(0.91, -10.18) * mm});
            skLineSegment(sketch, "E790", {"start": v(0.91, -10.18) * mm, "end": v(0.93, -10.11) * mm});
            skLineSegment(sketch, "E791", {"start": v(0.93, -10.11) * mm, "end": v(0.95, -10.05) * mm});
            skLineSegment(sketch, "E792", {"start": v(0.95, -10.05) * mm, "end": v(0.97, -9.99) * mm});
            skLineSegment(sketch, "E793", {"start": v(0.97, -9.99) * mm, "end": v(0.99, -9.93) * mm});
            skLineSegment(sketch, "E794", {"start": v(0.99, -9.93) * mm, "end": v(1, -9.88) * mm});
            skLineSegment(sketch, "E795", {"start": v(1, -9.88) * mm, "end": v(1.01, -9.82) * mm});
            skLineSegment(sketch, "E796", {"start": v(1.01, -9.82) * mm, "end": v(1.03, -9.75) * mm});
            skLineSegment(sketch, "E797", {"start": v(1.03, -9.75) * mm, "end": v(1.04, -9.68) * mm});
            skLineSegment(sketch, "E798", {"start": v(1.04, -9.68) * mm, "end": v(1.05, -9.62) * mm});
            skLineSegment(sketch, "E799", {"start": v(1.05, -9.62) * mm, "end": v(1.05, -9.56) * mm});
            skLineSegment(sketch, "E800", {"start": v(1.05, -9.56) * mm, "end": v(1.06, -9.5) * mm});
            skLineSegment(sketch, "E801", {"start": v(1.06, -9.5) * mm, "end": v(1.06, -9.44) * mm});
            skLineSegment(sketch, "E802", {"start": v(1.06, -9.44) * mm, "end": v(1.06, -9.39) * mm});
            skLineSegment(sketch, "E803", {"start": v(1.06, -9.39) * mm, "end": v(1.06, -9.34) * mm});
            skLineSegment(sketch, "E804", {"start": v(1.06, -9.34) * mm, "end": v(0.95, -8.38) * mm});
            skArc(sketch, "E805", {"start": v(0.95, -8.38) * mm, "mid": v(1.64, -8.25) * mm, "end": v(2.33, -8.1) * mm});
            skLineSegment(sketch, "E806", {"start": v(2.33, -8.1) * mm, "end": v(2.6, -9.03) * mm});
            skLineSegment(sketch, "E807", {"start": v(2.6, -9.03) * mm, "end": v(2.61, -9.08) * mm});
            skLineSegment(sketch, "E808", {"start": v(2.61, -9.08) * mm, "end": v(2.63, -9.13) * mm});
            skLineSegment(sketch, "E809", {"start": v(2.63, -9.13) * mm, "end": v(2.65, -9.18) * mm});
            skLineSegment(sketch, "E810", {"start": v(2.65, -9.18) * mm, "end": v(2.69, -9.24) * mm});
            skLineSegment(sketch, "E811", {"start": v(2.69, -9.24) * mm, "end": v(2.71, -9.29) * mm});
            skLineSegment(sketch, "E812", {"start": v(2.71, -9.29) * mm, "end": v(2.75, -9.34) * mm});
            skLineSegment(sketch, "E813", {"start": v(2.75, -9.34) * mm, "end": v(2.78, -9.4) * mm});
            skLineSegment(sketch, "E814", {"start": v(2.78, -9.4) * mm, "end": v(2.83, -9.46) * mm});
            skLineSegment(sketch, "E815", {"start": v(2.83, -9.46) * mm, "end": v(2.86, -9.5) * mm});
            skLineSegment(sketch, "E816", {"start": v(2.86, -9.5) * mm, "end": v(2.9, -9.55) * mm});
            skLineSegment(sketch, "E817", {"start": v(2.9, -9.55) * mm, "end": v(2.93, -9.6) * mm});
            skLineSegment(sketch, "E818", {"start": v(2.93, -9.6) * mm, "end": v(2.97, -9.65) * mm});
            skLineSegment(sketch, "E819", {"start": v(2.97, -9.65) * mm, "end": v(3, -9.7) * mm});
            skLineSegment(sketch, "E820", {"start": v(3, -9.7) * mm, "end": v(3.05, -9.75) * mm});
            skLineSegment(sketch, "E821", {"start": v(3.05, -9.75) * mm, "end": v(3.1, -9.8) * mm});
            skLineSegment(sketch, "E822", {"start": v(3.1, -9.8) * mm, "end": v(3.15, -9.86) * mm});
            skLineSegment(sketch, "E823", {"start": v(3.15, -9.86) * mm, "end": v(3.2, -9.92) * mm});
            skLineSegment(sketch, "E824", {"start": v(3.2, -9.92) * mm, "end": v(3.26, -9.98) * mm});
            skLineSegment(sketch, "E825", {"start": v(3.26, -9.98) * mm, "end": v(3.31, -10.04) * mm});
            skLineSegment(sketch, "E826", {"start": v(3.31, -10.04) * mm, "end": v(3.38, -10.1) * mm});
            skLineSegment(sketch, "E827", {"start": v(3.38, -10.1) * mm, "end": v(3.44, -10.16) * mm});
            skLineSegment(sketch, "E828", {"start": v(3.44, -10.16) * mm, "end": v(3.5, -10.22) * mm});
            skLineSegment(sketch, "E829", {"start": v(3.5, -10.22) * mm, "end": v(3.58, -10.28) * mm});
            skLineSegment(sketch, "E830", {"start": v(3.58, -10.28) * mm, "end": v(3.66, -10.34) * mm});
            skLineSegment(sketch, "E831", {"start": v(3.66, -10.34) * mm, "end": v(3.73, -10.4) * mm});
            skLineSegment(sketch, "E832", {"start": v(3.73, -10.4) * mm, "end": v(3.77, -10.44) * mm});
            skLineSegment(sketch, "E833", {"start": v(3.77, -10.44) * mm, "end": v(3.81, -10.47) * mm});
            skLineSegment(sketch, "E834", {"start": v(3.81, -10.47) * mm, "end": v(3.86, -10.5) * mm});
            skLineSegment(sketch, "E835", {"start": v(3.86, -10.5) * mm, "end": v(3.92, -10.55) * mm});
            skLineSegment(sketch, "E836", {"start": v(3.92, -10.55) * mm, "end": v(4.69, -10.23) * mm});
            skLineSegment(sketch, "E837", {"start": v(4.69, -10.23) * mm, "end": v(4.7, -10.15) * mm});
            skLineSegment(sketch, "E838", {"start": v(4.7, -10.15) * mm, "end": v(4.7, -10.1) * mm});
            skLineSegment(sketch, "E839", {"start": v(4.7, -10.1) * mm, "end": v(4.71, -10.05) * mm});
            skLineSegment(sketch, "E840", {"start": v(4.71, -10.05) * mm, "end": v(4.72, -10) * mm});
            skLineSegment(sketch, "E841", {"start": v(4.72, -10) * mm, "end": v(4.73, -9.9) * mm});
            skLineSegment(sketch, "E842", {"start": v(4.73, -9.9) * mm, "end": v(4.74, -9.8) * mm});
            skLineSegment(sketch, "E843", {"start": v(4.74, -9.8) * mm, "end": v(4.74, -9.7) * mm});
            skLineSegment(sketch, "E844", {"start": v(4.74, -9.7) * mm, "end": v(4.75, -9.62) * mm});
            skLineSegment(sketch, "E845", {"start": v(4.75, -9.62) * mm, "end": v(4.75, -9.53) * mm});
            skLineSegment(sketch, "E846", {"start": v(4.75, -9.53) * mm, "end": v(4.75, -9.44) * mm});
            skLineSegment(sketch, "E847", {"start": v(4.75, -9.44) * mm, "end": v(4.75, -9.36) * mm});
            skLineSegment(sketch, "E848", {"start": v(4.75, -9.36) * mm, "end": v(4.75, -9.28) * mm});
            skLineSegment(sketch, "E849", {"start": v(4.75, -9.28) * mm, "end": v(4.75, -9.2) * mm});
            skLineSegment(sketch, "E850", {"start": v(4.75, -9.2) * mm, "end": v(4.74, -9.13) * mm});
            skLineSegment(sketch, "E851", {"start": v(4.74, -9.13) * mm, "end": v(4.74, -9.05) * mm});
            skLineSegment(sketch, "E852", {"start": v(4.74, -9.05) * mm, "end": v(4.73, -8.99) * mm});
            skLineSegment(sketch, "E853", {"start": v(4.73, -8.99) * mm, "end": v(4.73, -8.92) * mm});
            skLineSegment(sketch, "E854", {"start": v(4.73, -8.92) * mm, "end": v(4.72, -8.86) * mm});
            skLineSegment(sketch, "E855", {"start": v(4.72, -8.86) * mm, "end": v(4.71, -8.8) * mm});
            skLineSegment(sketch, "E856", {"start": v(4.71, -8.8) * mm, "end": v(4.7, -8.74) * mm});
            skLineSegment(sketch, "E857", {"start": v(4.7, -8.74) * mm, "end": v(4.7, -8.69) * mm});
            skLineSegment(sketch, "E858", {"start": v(4.7, -8.69) * mm, "end": v(4.68, -8.61) * mm});
            skLineSegment(sketch, "E859", {"start": v(4.68, -8.61) * mm, "end": v(4.66, -8.55) * mm});
            skLineSegment(sketch, "E860", {"start": v(4.66, -8.55) * mm, "end": v(4.65, -8.48) * mm});
            skLineSegment(sketch, "E861", {"start": v(4.65, -8.48) * mm, "end": v(4.63, -8.43) * mm});
            skLineSegment(sketch, "E862", {"start": v(4.63, -8.43) * mm, "end": v(4.61, -8.37) * mm});
            skLineSegment(sketch, "E863", {"start": v(4.61, -8.37) * mm, "end": v(4.6, -8.32) * mm});
            skLineSegment(sketch, "E864", {"start": v(4.6, -8.32) * mm, "end": v(4.57, -8.27) * mm});
            skLineSegment(sketch, "E865", {"start": v(4.57, -8.27) * mm, "end": v(4.55, -8.22) * mm});
            skLineSegment(sketch, "E866", {"start": v(4.55, -8.22) * mm, "end": v(4.09, -7.38) * mm});
            skArc(sketch, "E867", {"start": v(4.09, -7.38) * mm, "mid": v(4.67, -7) * mm, "end": v(5.25, -6.6) * mm});
            skLineSegment(sketch, "E868", {"start": v(5.25, -6.6) * mm, "end": v(5.85, -7.35) * mm});
            skLineSegment(sketch, "E869", {"start": v(5.85, -7.35) * mm, "end": v(5.89, -7.39) * mm});
            skLineSegment(sketch, "E870", {"start": v(5.89, -7.39) * mm, "end": v(5.92, -7.43) * mm});
            skLineSegment(sketch, "E871", {"start": v(5.92, -7.43) * mm, "end": v(5.96, -7.46) * mm});
            skLineSegment(sketch, "E872", {"start": v(5.96, -7.46) * mm, "end": v(6.02, -7.5) * mm});
            skLineSegment(sketch, "E873", {"start": v(6.02, -7.5) * mm, "end": v(6.06, -7.54) * mm});
            skLineSegment(sketch, "E874", {"start": v(6.06, -7.54) * mm, "end": v(6.11, -7.58) * mm});
            skLineSegment(sketch, "E875", {"start": v(6.11, -7.58) * mm, "end": v(6.17, -7.62) * mm});
            skLineSegment(sketch, "E876", {"start": v(6.17, -7.62) * mm, "end": v(6.23, -7.66) * mm});
            skLineSegment(sketch, "E877", {"start": v(6.23, -7.66) * mm, "end": v(6.28, -7.69) * mm});
            skLineSegment(sketch, "E878", {"start": v(6.28, -7.69) * mm, "end": v(6.33, -7.72) * mm});
            skLineSegment(sketch, "E879", {"start": v(6.33, -7.72) * mm, "end": v(6.38, -7.75) * mm});
            skLineSegment(sketch, "E880", {"start": v(6.38, -7.75) * mm, "end": v(6.43, -7.78) * mm});
            skLineSegment(sketch, "E881", {"start": v(6.43, -7.78) * mm, "end": v(6.5, -7.81) * mm});
            skLineSegment(sketch, "E882", {"start": v(6.5, -7.81) * mm, "end": v(6.55, -7.84) * mm});
            skLineSegment(sketch, "E883", {"start": v(6.55, -7.84) * mm, "end": v(6.62, -7.88) * mm});
            skLineSegment(sketch, "E884", {"start": v(6.62, -7.88) * mm, "end": v(6.68, -7.9) * mm});
            skLineSegment(sketch, "E885", {"start": v(6.68, -7.9) * mm, "end": v(6.75, -7.94) * mm});
            skLineSegment(sketch, "E886", {"start": v(6.75, -7.94) * mm, "end": v(6.83, -7.97) * mm});
            skLineSegment(sketch, "E887", {"start": v(6.83, -7.97) * mm, "end": v(6.9, -8) * mm});
            skLineSegment(sketch, "E888", {"start": v(6.9, -8) * mm, "end": v(6.98, -8.04) * mm});
            skLineSegment(sketch, "E889", {"start": v(6.98, -8.04) * mm, "end": v(7.07, -8.07) * mm});
            skLineSegment(sketch, "E890", {"start": v(7.07, -8.07) * mm, "end": v(7.15, -8.1) * mm});
            skLineSegment(sketch, "E891", {"start": v(7.15, -8.1) * mm, "end": v(7.24, -8.13) * mm});
            skLineSegment(sketch, "E892", {"start": v(7.24, -8.13) * mm, "end": v(7.33, -8.16) * mm});
            skLineSegment(sketch, "E893", {"start": v(7.33, -8.16) * mm, "end": v(7.43, -8.18) * mm});
            skLineSegment(sketch, "E894", {"start": v(7.43, -8.18) * mm, "end": v(7.48, -8.2) * mm});
            skLineSegment(sketch, "E895", {"start": v(7.48, -8.2) * mm, "end": v(7.53, -8.21) * mm});
            skLineSegment(sketch, "E896", {"start": v(7.53, -8.21) * mm, "end": v(7.58, -8.23) * mm});
            skLineSegment(sketch, "E897", {"start": v(7.58, -8.23) * mm, "end": v(7.66, -8.24) * mm});
            skLineSegment(sketch, "E898", {"start": v(7.66, -8.24) * mm, "end": v(8.24, -7.66) * mm});
            skLineSegment(sketch, "E899", {"start": v(8.24, -7.66) * mm, "end": v(8.23, -7.58) * mm});
            skLineSegment(sketch, "E900", {"start": v(8.23, -7.58) * mm, "end": v(8.21, -7.53) * mm});
            skLineSegment(sketch, "E901", {"start": v(8.21, -7.53) * mm, "end": v(8.2, -7.48) * mm});
            skLineSegment(sketch, "E902", {"start": v(8.2, -7.48) * mm, "end": v(8.18, -7.43) * mm});
            skLineSegment(sketch, "E903", {"start": v(8.18, -7.43) * mm, "end": v(8.16, -7.33) * mm});
            skLineSegment(sketch, "E904", {"start": v(8.16, -7.33) * mm, "end": v(8.13, -7.24) * mm});
            skLineSegment(sketch, "E905", {"start": v(8.13, -7.24) * mm, "end": v(8.1, -7.15) * mm});
            skLineSegment(sketch, "E906", {"start": v(8.1, -7.15) * mm, "end": v(8.07, -7.07) * mm});
            skLineSegment(sketch, "E907", {"start": v(8.07, -7.07) * mm, "end": v(8.04, -6.98) * mm});
            skLineSegment(sketch, "E908", {"start": v(8.04, -6.98) * mm, "end": v(8, -6.9) * mm});
            skLineSegment(sketch, "E909", {"start": v(8, -6.9) * mm, "end": v(7.97, -6.83) * mm});
            skLineSegment(sketch, "E910", {"start": v(7.97, -6.83) * mm, "end": v(7.94, -6.75) * mm});
            skLineSegment(sketch, "E911", {"start": v(7.94, -6.75) * mm, "end": v(7.9, -6.68) * mm});
            skLineSegment(sketch, "E912", {"start": v(7.9, -6.68) * mm, "end": v(7.88, -6.62) * mm});
            skLineSegment(sketch, "E913", {"start": v(7.88, -6.62) * mm, "end": v(7.84, -6.55) * mm});
            skLineSegment(sketch, "E914", {"start": v(7.84, -6.55) * mm, "end": v(7.81, -6.5) * mm});
            skLineSegment(sketch, "E915", {"start": v(7.81, -6.5) * mm, "end": v(7.78, -6.43) * mm});
            skLineSegment(sketch, "E916", {"start": v(7.78, -6.43) * mm, "end": v(7.75, -6.38) * mm});
            skLineSegment(sketch, "E917", {"start": v(7.75, -6.38) * mm, "end": v(7.72, -6.33) * mm});
            skLineSegment(sketch, "E918", {"start": v(7.72, -6.33) * mm, "end": v(7.69, -6.28) * mm});
            skLineSegment(sketch, "E919", {"start": v(7.69, -6.28) * mm, "end": v(7.66, -6.23) * mm});
            skLineSegment(sketch, "E920", {"start": v(7.66, -6.23) * mm, "end": v(7.62, -6.17) * mm});
            skLineSegment(sketch, "E921", {"start": v(7.62, -6.17) * mm, "end": v(7.58, -6.11) * mm});
            skLineSegment(sketch, "E922", {"start": v(7.58, -6.11) * mm, "end": v(7.54, -6.06) * mm});
            skLineSegment(sketch, "E923", {"start": v(7.54, -6.06) * mm, "end": v(7.5, -6.02) * mm});
            skLineSegment(sketch, "E924", {"start": v(7.5, -6.02) * mm, "end": v(7.46, -5.96) * mm});
            skLineSegment(sketch, "E925", {"start": v(7.46, -5.96) * mm, "end": v(7.43, -5.92) * mm});
            skLineSegment(sketch, "E926", {"start": v(7.43, -5.92) * mm, "end": v(7.39, -5.89) * mm});
            skLineSegment(sketch, "E927", {"start": v(7.39, -5.89) * mm, "end": v(7.35, -5.85) * mm});
            skLineSegment(sketch, "E928", {"start": v(7.35, -5.85) * mm, "end": v(6.6, -5.25) * mm});
            skArc(sketch, "E929", {"start": v(6.6, -5.25) * mm, "mid": v(7, -4.67) * mm, "end": v(7.38, -4.09) * mm});
            skLineSegment(sketch, "E930", {"start": v(7.38, -4.09) * mm, "end": v(8.22, -4.55) * mm});
            skLineSegment(sketch, "E931", {"start": v(8.22, -4.55) * mm, "end": v(8.27, -4.57) * mm});
            skLineSegment(sketch, "E932", {"start": v(8.27, -4.57) * mm, "end": v(8.32, -4.6) * mm});
            skLineSegment(sketch, "E933", {"start": v(8.32, -4.6) * mm, "end": v(8.37, -4.61) * mm});
            skLineSegment(sketch, "E934", {"start": v(8.37, -4.61) * mm, "end": v(8.43, -4.63) * mm});
            skLineSegment(sketch, "E935", {"start": v(8.43, -4.63) * mm, "end": v(8.48, -4.65) * mm});
            skLineSegment(sketch, "E936", {"start": v(8.48, -4.65) * mm, "end": v(8.55, -4.66) * mm});
            skLineSegment(sketch, "E937", {"start": v(8.55, -4.66) * mm, "end": v(8.61, -4.68) * mm});
            skLineSegment(sketch, "E938", {"start": v(8.61, -4.68) * mm, "end": v(8.69, -4.7) * mm});
            skLineSegment(sketch, "E939", {"start": v(8.69, -4.7) * mm, "end": v(8.74, -4.7) * mm});
            skLineSegment(sketch, "E940", {"start": v(8.74, -4.7) * mm, "end": v(8.8, -4.71) * mm});
            skLineSegment(sketch, "E941", {"start": v(8.8, -4.71) * mm, "end": v(8.86, -4.72) * mm});
            skLineSegment(sketch, "E942", {"start": v(8.86, -4.72) * mm, "end": v(8.92, -4.73) * mm});
            skLineSegment(sketch, "E943", {"start": v(8.92, -4.73) * mm, "end": v(8.99, -4.73) * mm});
            skLineSegment(sketch, "E944", {"start": v(8.99, -4.73) * mm, "end": v(9.05, -4.74) * mm});
            skLineSegment(sketch, "E945", {"start": v(9.05, -4.74) * mm, "end": v(9.13, -4.74) * mm});
            skLineSegment(sketch, "E946", {"start": v(9.13, -4.74) * mm, "end": v(9.2, -4.75) * mm});
            skLineSegment(sketch, "E947", {"start": v(9.2, -4.75) * mm, "end": v(9.28, -4.75) * mm});
            skLineSegment(sketch, "E948", {"start": v(9.28, -4.75) * mm, "end": v(9.36, -4.75) * mm});
            skLineSegment(sketch, "E949", {"start": v(9.36, -4.75) * mm, "end": v(9.44, -4.75) * mm});
            skLineSegment(sketch, "E950", {"start": v(9.44, -4.75) * mm, "end": v(9.53, -4.75) * mm});
            skLineSegment(sketch, "E951", {"start": v(9.53, -4.75) * mm, "end": v(9.62, -4.75) * mm});
            skLineSegment(sketch, "E952", {"start": v(9.62, -4.75) * mm, "end": v(9.7, -4.74) * mm});
            skLineSegment(sketch, "E953", {"start": v(9.7, -4.74) * mm, "end": v(9.8, -4.74) * mm});
            skLineSegment(sketch, "E954", {"start": v(9.8, -4.74) * mm, "end": v(9.9, -4.73) * mm});
            skLineSegment(sketch, "E955", {"start": v(9.9, -4.73) * mm, "end": v(10, -4.72) * mm});
            skLineSegment(sketch, "E956", {"start": v(10, -4.72) * mm, "end": v(10.05, -4.71) * mm});
            skLineSegment(sketch, "E957", {"start": v(10.05, -4.71) * mm, "end": v(10.1, -4.7) * mm});
            skLineSegment(sketch, "E958", {"start": v(10.1, -4.7) * mm, "end": v(10.15, -4.7) * mm});
            skLineSegment(sketch, "E959", {"start": v(10.15, -4.7) * mm, "end": v(10.23, -4.69) * mm});
            skLineSegment(sketch, "E960", {"start": v(10.23, -4.69) * mm, "end": v(10.55, -3.92) * mm});
            skLineSegment(sketch, "E961", {"start": v(10.55, -3.92) * mm, "end": v(10.5, -3.86) * mm});
            skLineSegment(sketch, "E962", {"start": v(10.5, -3.86) * mm, "end": v(10.47, -3.81) * mm});
            skLineSegment(sketch, "E963", {"start": v(10.47, -3.81) * mm, "end": v(10.44, -3.77) * mm});
            skLineSegment(sketch, "E964", {"start": v(10.44, -3.77) * mm, "end": v(10.4, -3.73) * mm});
            skLineSegment(sketch, "E965", {"start": v(10.4, -3.73) * mm, "end": v(10.34, -3.66) * mm});
            skLineSegment(sketch, "E966", {"start": v(10.34, -3.66) * mm, "end": v(10.28, -3.58) * mm});
            skLineSegment(sketch, "E967", {"start": v(10.28, -3.58) * mm, "end": v(10.22, -3.5) * mm});
            skLineSegment(sketch, "E968", {"start": v(10.22, -3.5) * mm, "end": v(10.16, -3.44) * mm});
            skLineSegment(sketch, "E969", {"start": v(10.16, -3.44) * mm, "end": v(10.1, -3.38) * mm});
            skLineSegment(sketch, "E970", {"start": v(10.1, -3.38) * mm, "end": v(10.04, -3.31) * mm});
            skLineSegment(sketch, "E971", {"start": v(10.04, -3.31) * mm, "end": v(9.98, -3.26) * mm});
            skLineSegment(sketch, "E972", {"start": v(9.98, -3.26) * mm, "end": v(9.92, -3.2) * mm});
            skLineSegment(sketch, "E973", {"start": v(9.92, -3.2) * mm, "end": v(9.86, -3.15) * mm});
            skLineSegment(sketch, "E974", {"start": v(9.86, -3.15) * mm, "end": v(9.8, -3.1) * mm});
            skLineSegment(sketch, "E975", {"start": v(9.8, -3.1) * mm, "end": v(9.75, -3.05) * mm});
            skLineSegment(sketch, "E976", {"start": v(9.75, -3.05) * mm, "end": v(9.7, -3) * mm});
            skLineSegment(sketch, "E977", {"start": v(9.7, -3) * mm, "end": v(9.65, -2.97) * mm});
            skLineSegment(sketch, "E978", {"start": v(9.65, -2.97) * mm, "end": v(9.6, -2.93) * mm});
            skLineSegment(sketch, "E979", {"start": v(9.6, -2.93) * mm, "end": v(9.55, -2.9) * mm});
            skLineSegment(sketch, "E980", {"start": v(9.55, -2.9) * mm, "end": v(9.5, -2.86) * mm});
            skLineSegment(sketch, "E981", {"start": v(9.5, -2.86) * mm, "end": v(9.46, -2.83) * mm});
            skLineSegment(sketch, "E982", {"start": v(9.46, -2.83) * mm, "end": v(9.4, -2.78) * mm});
            skLineSegment(sketch, "E983", {"start": v(9.4, -2.78) * mm, "end": v(9.34, -2.75) * mm});
            skLineSegment(sketch, "E984", {"start": v(9.34, -2.75) * mm, "end": v(9.29, -2.71) * mm});
            skLineSegment(sketch, "E985", {"start": v(9.29, -2.71) * mm, "end": v(9.24, -2.69) * mm});
            skLineSegment(sketch, "E986", {"start": v(9.24, -2.69) * mm, "end": v(9.18, -2.65) * mm});
            skLineSegment(sketch, "E987", {"start": v(9.18, -2.65) * mm, "end": v(9.13, -2.63) * mm});
            skLineSegment(sketch, "E988", {"start": v(9.13, -2.63) * mm, "end": v(9.08, -2.61) * mm});
            skLineSegment(sketch, "E989", {"start": v(9.08, -2.61) * mm, "end": v(9.03, -2.6) * mm});
            skLineSegment(sketch, "E990", {"start": v(9.03, -2.6) * mm, "end": v(8.1, -2.33) * mm});
            skArc(sketch, "E991", {"start": v(8.1, -2.33) * mm, "mid": v(8.25, -1.64) * mm, "end": v(8.38, -0.95) * mm});
            skCircle(sketch, "E992", {"center": v(0, 0) * mm, "radius": 1.5 * mm});
            skSolve(sketch);
        }
        {
            var Q0;
            Q0=makeQuery(id+"F0.imprint","IMPRINT",FACE,{"disambiguationData":[TD([[makeQuery(id+"F0.imprint","IMPRINT",EDGE,{"derivedFrom":sQuery(id+"F0.wireOp",EDGE,"E0")}),1.0]])]});
            extrude(context, id + "F1", {"entities" : qUnion([Q0]), "depth" : 6 * mm});
        }
    });
